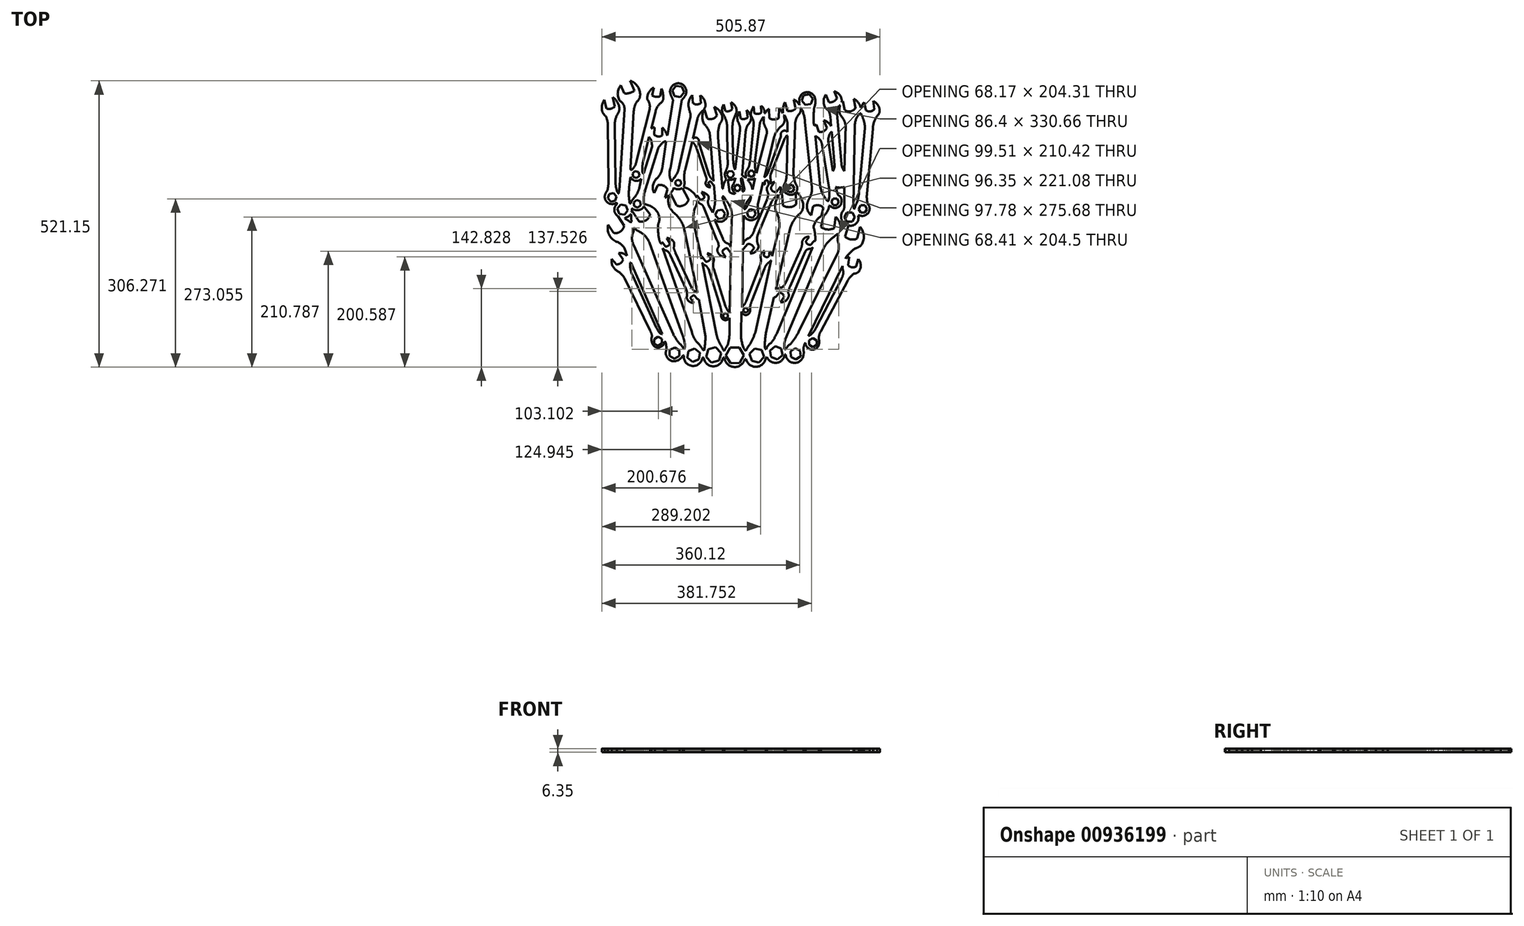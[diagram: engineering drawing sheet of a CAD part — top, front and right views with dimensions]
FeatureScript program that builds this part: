
annotation { "Feature Type Name" : "Feature", "Feature Type Description" : "" }
export const myFeature = defineFeature(function(context is Context, id is Id, definition is map)
    precondition{}
    {
        {
            var Q0;
            Q0=qCreatedBy(makeId("Top.planeOp"),FACE);
            var sketch = newSketch(context, id + "F0", { "sketchPlane" : qUnion([Q0])});
            skArc(sketch, "E0", {"start": v(348.41, 319.52) * mm, "mid": v(345.14, 328.83) * mm, "end": v(339.54, 336.96) * mm});
            skArc(sketch, "E1", {"start": v(301.1, 338.35) * mm, "mid": v(296.53, 329.72) * mm, "end": v(294.36, 320.2) * mm});
            skArc(sketch, "E2", {"start": v(337.47, 296.03) * mm, "mid": v(341.94, 301.33) * mm, "end": v(345.43, 307.32) * mm});
            skArc(sketch, "E3", {"start": v(337.47, 296.03) * mm, "mid": v(335.23, 290) * mm, "end": v(333.28, 283.88) * mm});
            skArc(sketch, "E4", {"start": v(334.87, 283.44) * mm, "mid": v(339.87, 290.96) * mm, "end": v(344.13, 298.93) * mm});
            skArc(sketch, "E5", {"start": v(296.24, 306.6) * mm, "mid": v(300.74, 298.9) * mm, "end": v(305.79, 291.55) * mm});
            skArc(sketch, "E6", {"start": v(310.85, 274.47) * mm, "mid": v(309.33, 283.31) * mm, "end": v(305.79, 291.55) * mm});
            skArc(sketch, "E7", {"start": v(306.8, 314.26) * mm, "mid": v(311.46, 312) * mm, "end": v(316.64, 311.85) * mm});
            skArc(sketch, "E8", {"start": v(330.67, 315.56) * mm, "mid": v(332.7, 316.57) * mm, "end": v(333.7, 318.6) * mm});
            skArc(sketch, "E9", {"start": v(344.13, 298.93) * mm, "mid": v(345.23, 303.05) * mm, "end": v(345.43, 307.32) * mm});
            skArc(sketch, "E10", {"start": v(293.49, 306.6) * mm, "mid": v(296.8, 294.77) * mm, "end": v(301.16, 283.3) * mm});
            skArc(sketch, "E11", {"start": v(294.65, 261.6) * mm, "mid": v(302.74, 271) * mm, "end": v(301.16, 283.3) * mm});
            skArc(sketch, "E12", {"start": v(279.6, 264.35) * mm, "mid": v(286.74, 260.86) * mm, "end": v(294.65, 261.6) * mm});
            skArc(sketch, "E13", {"start": v(276.27, 277.08) * mm, "mid": v(278.22, 284.26) * mm, "end": v(279.74, 291.55) * mm});
            skArc(sketch, "E14", {"start": v(279.74, 291.55) * mm, "mid": v(280.35, 299.07) * mm, "end": v(279.74, 306.6) * mm});
            skArc(sketch, "E15", {"start": v(268.46, 307.32) * mm, "mid": v(262.9, 312.12) * mm, "end": v(256.01, 314.7) * mm});
            skArc(sketch, "E16", {"start": v(267.59, 298.93) * mm, "mid": v(268.55, 303.07) * mm, "end": v(268.46, 307.32) * mm});
            skArc(sketch, "E17", {"start": v(267.59, 298.93) * mm, "mid": v(267.5, 294.82) * mm, "end": v(268.46, 290.82) * mm});
            skArc(sketch, "E18", {"start": v(253.56, 300.73) * mm, "mid": v(258.48, 302.2) * mm, "end": v(261.15, 306.6) * mm});
            skArc(sketch, "E19", {"start": v(247.62, 308.48) * mm, "mid": v(246.88, 306.78) * mm, "end": v(246.75, 304.93) * mm});
            skArc(sketch, "E20", {"start": v(247.98, 298.93) * mm, "mid": v(251.3, 294.76) * mm, "end": v(255.94, 292.13) * mm});
            skArc(sketch, "E21", {"start": v(259.34, 286.92) * mm, "mid": v(258, 289.76) * mm, "end": v(255.94, 292.13) * mm});
            skArc(sketch, "E22", {"start": v(313.82, 329.47) * mm, "mid": v(311.43, 321.31) * mm, "end": v(315.73, 313.98) * mm});
            skArc(sketch, "E23", {"start": v(313.82, 329.47) * mm, "mid": v(315.96, 334.73) * mm, "end": v(317.73, 340.13) * mm});
            skArc(sketch, "E24", {"start": v(327.58, 340.13) * mm, "mid": v(327.99, 333.31) * mm, "end": v(329.86, 326.74) * mm});
            skArc(sketch, "E25", {"start": v(330.22, 319.05) * mm, "mid": v(330.85, 322.93) * mm, "end": v(329.86, 326.74) * mm});
            skArc(sketch, "E26", {"start": v(303.54, 337.46) * mm, "mid": v(310.95, 337.13) * mm, "end": v(317.73, 340.13) * mm});
            skArc(sketch, "E27", {"start": v(298.87, 350.8) * mm, "mid": v(298.22, 344.26) * mm, "end": v(301.1, 338.35) * mm});
            skArc(sketch, "E28", {"start": v(298.87, 350.8) * mm, "mid": v(301.1, 356.06) * mm, "end": v(302.9, 361.48) * mm});
            skArc(sketch, "E29", {"start": v(313.82, 366.87) * mm, "mid": v(314.7, 360.94) * mm, "end": v(316.67, 355.27) * mm});
            skArc(sketch, "E30", {"start": v(339.35, 355.66) * mm, "mid": v(335.97, 349.35) * mm, "end": v(337.47, 342.35) * mm});
            skArc(sketch, "E31", {"start": v(340.94, 338.35) * mm, "mid": v(347.28, 337.45) * mm, "end": v(353.1, 340.13) * mm});
            skArc(sketch, "E32", {"start": v(353.24, 372.16) * mm, "mid": v(353.14, 360.37) * mm, "end": v(355.7, 348.86) * mm});
            skArc(sketch, "E33", {"start": v(339.35, 355.66) * mm, "mid": v(342.59, 363.96) * mm, "end": v(344.13, 372.73) * mm});
            skArc(sketch, "E34", {"start": v(302.9, 361.48) * mm, "mid": v(303.47, 368.7) * mm, "end": v(302.9, 375.92) * mm});
            skArc(sketch, "E35", {"start": v(312.8, 384.02) * mm, "mid": v(313, 375.43) * mm, "end": v(313.82, 366.87) * mm});
            skLineSegment(sketch, "E36", {"start": v(293.12, 324.7) * mm, "end": v(285.89, 414.11) * mm});
            skArc(sketch, "E37", {"start": v(289.21, 439.87) * mm, "mid": v(286.2, 427.16) * mm, "end": v(285.89, 414.11) * mm});
            skArc(sketch, "E38", {"start": v(289.21, 439.87) * mm, "mid": v(293.4, 447.66) * mm, "end": v(291.82, 456.36) * mm});
            skArc(sketch, "E39", {"start": v(291.82, 456.36) * mm, "mid": v(286.63, 464.31) * mm, "end": v(278.8, 469.67) * mm});
            skArc(sketch, "E40", {"start": v(266.06, 448.7) * mm, "mid": v(275.84, 447.87) * mm, "end": v(283.57, 453.9) * mm});
            skArc(sketch, "E41", {"start": v(260.71, 464.46) * mm, "mid": v(257.05, 451.39) * mm, "end": v(260.57, 438.28) * mm});
            skArc(sketch, "E42", {"start": v(270.55, 421.5) * mm, "mid": v(266.58, 430.5) * mm, "end": v(260.57, 438.28) * mm});
            skArc(sketch, "E43", {"start": v(271.56, 410.5) * mm, "mid": v(271.08, 416) * mm, "end": v(270.55, 421.5) * mm});
            skArc(sketch, "E44", {"start": v(296.16, 474.16) * mm, "mid": v(292.96, 464.62) * mm, "end": v(295.58, 454.91) * mm});
            skArc(sketch, "E45", {"start": v(302.1, 435.96) * mm, "mid": v(300.08, 445.87) * mm, "end": v(295.58, 454.91) * mm});
            skArc(sketch, "E46", {"start": v(319.6, 461.28) * mm, "mid": v(316.84, 471.13) * mm, "end": v(309.18, 477.92) * mm});
            skArc(sketch, "E47", {"start": v(319.6, 461.28) * mm, "mid": v(316.27, 452.84) * mm, "end": v(313.09, 444.35) * mm});
            skArc(sketch, "E48", {"start": v(313.09, 444.35) * mm, "mid": v(312.15, 437.27) * mm, "end": v(311.93, 430.13) * mm});
            skArc(sketch, "E49", {"start": v(324.69, 461.28) * mm, "mid": v(320.94, 451.94) * mm, "end": v(322.32, 441.98) * mm});
            skArc(sketch, "E50", {"start": v(345.93, 449.45) * mm, "mid": v(343.47, 457.32) * mm, "end": v(338, 463.49) * mm});
            skArc(sketch, "E51", {"start": v(326.79, 448.45) * mm, "mid": v(333.43, 447.49) * mm, "end": v(339.46, 450.46) * mm});
            skArc(sketch, "E52", {"start": v(340.96, 438.28) * mm, "mid": v(344.53, 443.38) * mm, "end": v(345.93, 449.45) * mm});
            skArc(sketch, "E53", {"start": v(340.96, 438.28) * mm, "mid": v(337.48, 431.75) * mm, "end": v(336.08, 424.49) * mm});
            skArc(sketch, "E54", {"start": v(325.79, 426.42) * mm, "mid": v(325.3, 434.48) * mm, "end": v(322.32, 441.98) * mm});
            skArc(sketch, "E55", {"start": v(350.58, 470.44) * mm, "mid": v(346.67, 463.13) * mm, "end": v(345.52, 454.91) * mm});
            skArc(sketch, "E56", {"start": v(370.45, 458.52) * mm, "mid": v(368.89, 465.9) * mm, "end": v(363.98, 471.64) * mm});
            skArc(sketch, "E57", {"start": v(368.54, 451.86) * mm, "mid": v(364.68, 446.11) * mm, "end": v(361.7, 439.87) * mm});
            skArc(sketch, "E58", {"start": v(378.38, 465.9) * mm, "mid": v(374.32, 462.84) * mm, "end": v(371.82, 458.43) * mm});
            skArc(sketch, "E59", {"start": v(402.9, 458.52) * mm, "mid": v(400.52, 463.04) * mm, "end": v(396.8, 466.54) * mm});
            skArc(sketch, "E60", {"start": v(378.84, 449.45) * mm, "mid": v(387.63, 446.57) * mm, "end": v(396.43, 449.45) * mm});
            skArc(sketch, "E61", {"start": v(351.86, 458.06) * mm, "mid": v(358.26, 456.75) * mm, "end": v(364.25, 459.34) * mm});
            skArc(sketch, "E62", {"start": v(350.58, 436.37) * mm, "mid": v(350.13, 443.75) * mm, "end": v(347.3, 450.59) * mm});
            skArc(sketch, "E63", {"start": v(345.52, 454.91) * mm, "mid": v(346.34, 452.72) * mm, "end": v(347.3, 450.59) * mm});
            skArc(sketch, "E64", {"start": v(369.28, 449.45) * mm, "mid": v(368.87, 440.63) * mm, "end": v(372.18, 432.45) * mm});
            skArc(sketch, "E65", {"start": v(374.19, 419.5) * mm, "mid": v(374.4, 426.17) * mm, "end": v(372.18, 432.45) * mm});
            skArc(sketch, "E66", {"start": v(399.98, 434) * mm, "mid": v(392.86, 425.57) * mm, "end": v(387.95, 415.68) * mm});
            skArc(sketch, "E67", {"start": v(399.98, 434) * mm, "mid": v(403.78, 437.5) * mm, "end": v(406.36, 441.98) * mm});
            skArc(sketch, "E68", {"start": v(406.36, 441.98) * mm, "mid": v(406.7, 447.8) * mm, "end": v(405.18, 453.41) * mm});
            skArc(sketch, "E69", {"start": v(412.29, 438.28) * mm, "mid": v(410.3, 446.94) * mm, "end": v(406.36, 454.91) * mm});
            skArc(sketch, "E70", {"start": v(431.7, 454.91) * mm, "mid": v(427.44, 446.06) * mm, "end": v(425.78, 436.37) * mm});
            skArc(sketch, "E71", {"start": v(431.7, 454.91) * mm, "mid": v(435.63, 460.62) * mm, "end": v(436.08, 467.54) * mm});
            skArc(sketch, "E72", {"start": v(407.37, 478.2) * mm, "mid": v(404.3, 469.07) * mm, "end": v(404.08, 459.43) * mm});
            skArc(sketch, "E73", {"start": v(412.29, 462.34) * mm, "mid": v(420.27, 462.54) * mm, "end": v(426.96, 466.9) * mm});
            skArc(sketch, "E74", {"start": v(433.78, 473.03) * mm, "mid": v(429.5, 479.16) * mm, "end": v(423.3, 483.37) * mm});
            skArc(sketch, "E75", {"start": v(433.66, 482.22) * mm, "mid": v(433.42, 478.39) * mm, "end": v(434.24, 474.64) * mm});
            skArc(sketch, "E76", {"start": v(462.49, 484.05) * mm, "mid": v(447.22, 496.46) * mm, "end": v(433.66, 482.22) * mm});
            skArc(sketch, "E77", {"start": v(460.53, 467.06) * mm, "mid": v(462.58, 475.43) * mm, "end": v(462.49, 484.05) * mm});
            skArc(sketch, "E78", {"start": v(460.53, 467.06) * mm, "mid": v(459.75, 453.95) * mm, "end": v(459.76, 440.82) * mm});
            skArc(sketch, "E79", {"start": v(444.03, 441.57) * mm, "mid": v(441.93, 455.04) * mm, "end": v(436.85, 467.7) * mm});
            skLineSegment(sketch, "E80", {"start": v(487.6, 478.07) * mm, "end": v(482.07, 492.23) * mm});
            skLineSegment(sketch, "E81", {"start": v(502, 485.54) * mm, "end": v(497.12, 498.05) * mm});
            skArc(sketch, "E82", {"start": v(482.07, 492.23) * mm, "mid": v(477.94, 481.37) * mm, "end": v(480.01, 469.94) * mm});
            skArc(sketch, "E83", {"start": v(510.73, 483.24) * mm, "mid": v(506.12, 492.67) * mm, "end": v(497.12, 498.05) * mm});
            skArc(sketch, "E84", {"start": v(487.6, 478.07) * mm, "mid": v(495.95, 479.6) * mm, "end": v(502, 485.54) * mm});
            skArc(sketch, "E85", {"start": v(480.01, 469.94) * mm, "mid": v(482.45, 466.43) * mm, "end": v(486.03, 464.1) * mm});
            skArc(sketch, "E86", {"start": v(510.73, 478.87) * mm, "mid": v(510.92, 481.06) * mm, "end": v(510.73, 483.24) * mm});
            skArc(sketch, "E87", {"start": v(506.35, 472.22) * mm, "mid": v(503.02, 464.98) * mm, "end": v(502, 457.09) * mm});
            skArc(sketch, "E88", {"start": v(490.04, 452.53) * mm, "mid": v(488.6, 458.51) * mm, "end": v(486.03, 464.1) * mm});
            skArc(sketch, "E89", {"start": v(508.08, 472.13) * mm, "mid": v(506.38, 462.88) * mm, "end": v(509.18, 453.9) * mm});
            skArc(sketch, "E90", {"start": v(516.2, 464.1) * mm, "mid": v(526.97, 461.6) * mm, "end": v(535.98, 468.02) * mm});
            skArc(sketch, "E91", {"start": v(545.36, 468.48) * mm, "mid": v(540.69, 477.86) * mm, "end": v(532.6, 484.52) * mm});
            skArc(sketch, "E92", {"start": v(551.56, 478.07) * mm, "mid": v(548.48, 473.5) * mm, "end": v(546.64, 468.3) * mm});
            skArc(sketch, "E93", {"start": v(517.84, 436.03) * mm, "mid": v(514.76, 445.57) * mm, "end": v(509.18, 453.9) * mm});
            skArc(sketch, "E94", {"start": v(543.81, 457.75) * mm, "mid": v(537.4, 448.01) * mm, "end": v(534.7, 436.67) * mm});
            skArc(sketch, "E95", {"start": v(546.1, 457.75) * mm, "mid": v(547.28, 454.14) * mm, "end": v(549.1, 450.8) * mm});
            skArc(sketch, "E96", {"start": v(553.2, 431.02) * mm, "mid": v(552, 441.08) * mm, "end": v(549.1, 450.8) * mm});
            skArc(sketch, "E97", {"start": v(575.44, 452.98) * mm, "mid": v(569.66, 442.09) * mm, "end": v(567.6, 429.92) * mm});
            skArc(sketch, "E98", {"start": v(575.44, 452.98) * mm, "mid": v(579.58, 459.64) * mm, "end": v(579.27, 467.48) * mm});
            skArc(sketch, "E99", {"start": v(579.27, 467.48) * mm, "mid": v(575.1, 475.08) * mm, "end": v(568.21, 480.33) * mm});
            skArc(sketch, "E100", {"start": v(555.02, 463.28) * mm, "mid": v(563, 461.47) * mm, "end": v(570.06, 465.56) * mm});
            skArc(sketch, "E101", {"start": v(491.17, 434.69) * mm, "mid": v(485.9, 441.28) * mm, "end": v(478.32, 445) * mm});
            skArc(sketch, "E102", {"start": v(469.3, 424.22) * mm, "mid": v(477.82, 425.25) * mm, "end": v(483.88, 431.33) * mm});
            skLineSegment(sketch, "E103", {"start": v(469.3, 424.22) * mm, "end": v(464.75, 437.26) * mm});
            skLineSegment(sketch, "E104", {"start": v(483.88, 431.33) * mm, "end": v(478.32, 445) * mm});
            skLineSegment(sketch, "E105", {"start": v(491.17, 434.69) * mm, "end": v(490.04, 452.53) * mm});
            skLineSegment(sketch, "E106", {"start": v(459.76, 440.82) * mm, "end": v(461.2, 435.27) * mm});
            skLineSegment(sketch, "E107", {"start": v(464.75, 437.26) * mm, "end": v(461.2, 435.27) * mm});
            skLineSegment(sketch, "E108", {"start": v(502, 457.09) * mm, "end": v(510.43, 365.53) * mm});
            skLineSegment(sketch, "E109", {"start": v(497.77, 363.22) * mm, "end": v(492.47, 424.42) * mm});
            skLineSegment(sketch, "E110", {"start": v(517.84, 436.03) * mm, "end": v(515.43, 353.09) * mm});
            skLineSegment(sketch, "E111", {"start": v(534.7, 436.67) * mm, "end": v(532.32, 291.07) * mm});
            skLineSegment(sketch, "E112", {"start": v(542.45, 314.37) * mm, "end": v(553.2, 431.02) * mm});
            skLineSegment(sketch, "E113", {"start": v(567.6, 429.92) * mm, "end": v(556.7, 311.62) * mm});
            skLineSegment(sketch, "E114", {"start": v(494.85, 353.19) * mm, "end": v(486.7, 404.52) * mm});
            skLineSegment(sketch, "E115", {"start": v(474.87, 401.42) * mm, "end": v(487.96, 319.3) * mm});
            skLineSegment(sketch, "E116", {"start": v(471.93, 323.62) * mm, "end": v(462.81, 417.09) * mm});
            skLineSegment(sketch, "E117", {"start": v(444.03, 441.57) * mm, "end": v(456.39, 323.43) * mm});
            skArc(sketch, "E118", {"start": v(474.87, 401.42) * mm, "mid": v(472.33, 408.49) * mm, "end": v(467.39, 414.15) * mm});
            skArc(sketch, "E119", {"start": v(462.81, 417.09) * mm, "mid": v(465, 415.47) * mm, "end": v(467.39, 414.15) * mm});
            skArc(sketch, "E120", {"start": v(490.01, 422.07) * mm, "mid": v(486.83, 413.58) * mm, "end": v(486.7, 404.52) * mm});
            skArc(sketch, "E121", {"start": v(492.47, 424.42) * mm, "mid": v(491.1, 423.39) * mm, "end": v(490.01, 422.07) * mm});
            skArc(sketch, "E122", {"start": v(508.08, 472.13) * mm, "mid": v(507.23, 472.4) * mm, "end": v(506.35, 472.22) * mm});
            skArc(sketch, "E123", {"start": v(513.27, 479.88) * mm, "mid": v(511.9, 479.64) * mm, "end": v(510.73, 478.87) * mm});
            skLineSegment(sketch, "E124", {"start": v(513.27, 479.88) * mm, "end": v(516.2, 464.1) * mm});
            skLineSegment(sketch, "E125", {"start": v(535.98, 468.02) * mm, "end": v(532.6, 484.52) * mm});
            skLineSegment(sketch, "E126", {"start": v(545.36, 468.48) * mm, "end": v(546.64, 468.3) * mm});
            skLineSegment(sketch, "E127", {"start": v(543.81, 457.75) * mm, "end": v(546.1, 457.75) * mm});
            skLineSegment(sketch, "E128", {"start": v(555.02, 463.28) * mm, "end": v(551.56, 478.07) * mm});
            skLineSegment(sketch, "E129", {"start": v(570.06, 465.56) * mm, "end": v(568.21, 480.33) * mm});
            skLineSegment(sketch, "E130", {"start": v(436.85, 467.7) * mm, "end": v(436.08, 467.54) * mm});
            skLineSegment(sketch, "E131", {"start": v(434.24, 474.64) * mm, "end": v(433.78, 473.03) * mm});
            skLineSegment(sketch, "E132", {"start": v(426.96, 466.9) * mm, "end": v(423.3, 483.37) * mm});
            skLineSegment(sketch, "E133", {"start": v(412.29, 462.34) * mm, "end": v(407.37, 478.2) * mm});
            skLineSegment(sketch, "E134", {"start": v(404.08, 459.43) * mm, "end": v(402.9, 458.52) * mm});
            skLineSegment(sketch, "E135", {"start": v(406.36, 454.91) * mm, "end": v(405.18, 453.41) * mm});
            skLineSegment(sketch, "E136", {"start": v(396.43, 449.45) * mm, "end": v(396.8, 466.54) * mm});
            skLineSegment(sketch, "E137", {"start": v(378.84, 449.45) * mm, "end": v(378.38, 465.9) * mm});
            skLineSegment(sketch, "E138", {"start": v(425.78, 436.37) * mm, "end": v(423.1, 350.19) * mm});
            skLineSegment(sketch, "E139", {"start": v(410.85, 350.19) * mm, "end": v(411.98, 416.8) * mm});
            skLineSegment(sketch, "E140", {"start": v(412.29, 438.28) * mm, "end": v(412.29, 424.61) * mm});
            skArc(sketch, "E141", {"start": v(423.1, 350.19) * mm, "mid": v(423.95, 339.63) * mm, "end": v(427.1, 329.52) * mm});
            skArc(sketch, "E142", {"start": v(428.13, 315.16) * mm, "mid": v(429.89, 322.5) * mm, "end": v(427.1, 329.52) * mm});
            skArc(sketch, "E143", {"start": v(440.77, 287.6) * mm, "mid": v(437.57, 302.81) * mm, "end": v(428.13, 315.16) * mm});
            skArc(sketch, "E144", {"start": v(430.66, 272.1) * mm, "mid": v(437.52, 278.68) * mm, "end": v(440.77, 287.6) * mm});
            skArc(sketch, "E145", {"start": v(430.66, 272.1) * mm, "mid": v(422.74, 261.56) * mm, "end": v(417.23, 249.6) * mm});
            skArc(sketch, "E146", {"start": v(448.22, 293.75) * mm, "mid": v(448.68, 281.86) * mm, "end": v(455.51, 272.1) * mm});
            skArc(sketch, "E147", {"start": v(452.23, 303.5) * mm, "mid": v(449.82, 298.8) * mm, "end": v(448.22, 293.75) * mm});
            skArc(sketch, "E148", {"start": v(452.23, 303.5) * mm, "mid": v(455.86, 313.14) * mm, "end": v(456.39, 323.43) * mm});
            skArc(sketch, "E149", {"start": v(471.93, 323.62) * mm, "mid": v(476.88, 310) * mm, "end": v(485.22, 298.13) * mm});
            skArc(sketch, "E150", {"start": v(486.77, 299.31) * mm, "mid": v(488.46, 309.25) * mm, "end": v(487.96, 319.3) * mm});
            skArc(sketch, "E151", {"start": v(485.22, 298.13) * mm, "mid": v(486.23, 298.42) * mm, "end": v(486.77, 299.31) * mm});
            skArc(sketch, "E152", {"start": v(477.47, 285.72) * mm, "mid": v(468.21, 290.63) * mm, "end": v(458.18, 287.6) * mm});
            skArc(sketch, "E153", {"start": v(403.84, 290.12) * mm, "mid": v(416.36, 287.2) * mm, "end": v(428.13, 292.37) * mm});
            skArc(sketch, "E154", {"start": v(404.86, 323.43) * mm, "mid": v(412.52, 310.76) * mm, "end": v(427.1, 313.35) * mm});
            skArc(sketch, "E155", {"start": v(408.47, 333.02) * mm, "mid": v(406.08, 328.45) * mm, "end": v(404.86, 323.43) * mm});
            skArc(sketch, "E156", {"start": v(408.47, 333.02) * mm, "mid": v(410.18, 341.53) * mm, "end": v(410.85, 350.19) * mm});
            skArc(sketch, "E157", {"start": v(401.75, 313.43) * mm, "mid": v(400.29, 312.91) * mm, "end": v(398.85, 312.35) * mm});
            skArc(sketch, "E158", {"start": v(398.85, 312.35) * mm, "mid": v(400.24, 318.27) * mm, "end": v(399.36, 324.28) * mm});
            skArc(sketch, "E159", {"start": v(382.11, 323.43) * mm, "mid": v(385.04, 316.56) * mm, "end": v(392.38, 315.16) * mm});
            skArc(sketch, "E160", {"start": v(388.62, 333.02) * mm, "mid": v(384.26, 331.75) * mm, "end": v(380.3, 329.52) * mm});
            skArc(sketch, "E161", {"start": v(379.5, 330.14) * mm, "mid": v(381.54, 334.6) * mm, "end": v(380.88, 339.47) * mm});
            skArc(sketch, "E162", {"start": v(381.82, 347.21) * mm, "mid": v(380.86, 343.4) * mm, "end": v(380.88, 339.47) * mm});
            skArc(sketch, "E163", {"start": v(410.85, 417.67) * mm, "mid": v(408.91, 414.85) * mm, "end": v(407.21, 411.88) * mm});
            skArc(sketch, "E164", {"start": v(411.98, 424.25) * mm, "mid": v(405.3, 426.26) * mm, "end": v(400.27, 421.43) * mm});
            skArc(sketch, "E165", {"start": v(400.27, 421.43) * mm, "mid": v(399.81, 418.46) * mm, "end": v(400.27, 415.5) * mm});
            skArc(sketch, "E166", {"start": v(372.42, 343.47) * mm, "mid": v(371.17, 342.67) * mm, "end": v(370.03, 341.73) * mm});
            skArc(sketch, "E167", {"start": v(372.42, 343.47) * mm, "mid": v(374.38, 345.86) * mm, "end": v(375.67, 348.68) * mm});
            skArc(sketch, "E168", {"start": v(377.2, 334.79) * mm, "mid": v(374.06, 335.66) * mm, "end": v(370.97, 334.64) * mm});
            skArc(sketch, "E169", {"start": v(367.42, 332.25) * mm, "mid": v(368.62, 329.82) * mm, "end": v(370.68, 328.06) * mm});
            skArc(sketch, "E170", {"start": v(377.77, 327.48) * mm, "mid": v(374.55, 320.7) * mm, "end": v(376.76, 313.52) * mm});
            skArc(sketch, "E171", {"start": v(374.59, 300.2) * mm, "mid": v(376.5, 306.73) * mm, "end": v(376.76, 313.52) * mm});
            skArc(sketch, "E172", {"start": v(395.5, 309.03) * mm, "mid": v(388.15, 303.82) * mm, "end": v(382.98, 296.44) * mm});
            skArc(sketch, "E173", {"start": v(396.5, 307.87) * mm, "mid": v(390.36, 294.35) * mm, "end": v(391.3, 279.52) * mm});
            skArc(sketch, "E174", {"start": v(397.3, 251.01) * mm, "mid": v(396.3, 265.69) * mm, "end": v(391.3, 279.52) * mm});
            skArc(sketch, "E175", {"start": v(384.18, 198.36) * mm, "mid": v(382.62, 203.05) * mm, "end": v(379.54, 206.93) * mm});
            skArc(sketch, "E176", {"start": v(369.15, 198.9) * mm, "mid": v(373.53, 196.23) * mm, "end": v(378.53, 197.36) * mm});
            skArc(sketch, "E177", {"start": v(370.15, 207.75) * mm, "mid": v(363.78, 201.36) * mm, "end": v(363.95, 192.34) * mm});
            skArc(sketch, "E178", {"start": v(375.34, 184.41) * mm, "mid": v(379.03, 187.17) * mm, "end": v(382.09, 190.61) * mm});
            skArc(sketch, "E179", {"start": v(375.34, 184.41) * mm, "mid": v(372.38, 180.05) * mm, "end": v(370.06, 175.3) * mm});
            skArc(sketch, "E180", {"start": v(361.76, 180.5) * mm, "mid": v(363.42, 186.32) * mm, "end": v(363.95, 192.34) * mm});
            skArc(sketch, "E181", {"start": v(344.06, 202.97) * mm, "mid": v(354.7, 206.9) * mm, "end": v(359.54, 217.15) * mm});
            skArc(sketch, "E182", {"start": v(359.54, 239.58) * mm, "mid": v(356.64, 228.36) * mm, "end": v(359.54, 217.15) * mm});
            skArc(sketch, "E183", {"start": v(342.18, 230.6) * mm, "mid": v(334.85, 226.6) * mm, "end": v(331.04, 219.18) * mm});
            skArc(sketch, "E184", {"start": v(342.18, 230.6) * mm, "mid": v(348.26, 237.5) * mm, "end": v(351.88, 245.94) * mm});
            skArc(sketch, "E185", {"start": v(351.15, 212.66) * mm, "mid": v(346.78, 218.47) * mm, "end": v(339.72, 220.19) * mm});
            skArc(sketch, "E186", {"start": v(332.75, 272.1) * mm, "mid": v(346.84, 263.34) * mm, "end": v(359.54, 274.01) * mm});
            skArc(sketch, "E187", {"start": v(357.92, 291.95) * mm, "mid": v(358.2, 282.94) * mm, "end": v(359.54, 274.01) * mm});
            skArc(sketch, "E188", {"start": v(333.28, 283.88) * mm, "mid": v(334, 283.41) * mm, "end": v(334.87, 283.44) * mm});
            skArc(sketch, "E189", {"start": v(330.22, 319.05) * mm, "mid": v(330.21, 317.28) * mm, "end": v(330.67, 315.56) * mm});
            skArc(sketch, "E190", {"start": v(316.64, 311.85) * mm, "mid": v(316.48, 313.04) * mm, "end": v(315.73, 313.98) * mm});
            skLineSegment(sketch, "E191", {"start": v(455.51, 272.1) * mm, "end": v(458.18, 287.6) * mm});
            skLineSegment(sketch, "E192", {"start": v(403.84, 290.12) * mm, "end": v(401.75, 313.43) * mm});
            skLineSegment(sketch, "E193", {"start": v(428.13, 292.37) * mm, "end": v(427.1, 313.35) * mm});
            skLineSegment(sketch, "E194", {"start": v(392.38, 315.16) * mm, "end": v(399.36, 324.28) * mm});
            skLineSegment(sketch, "E195", {"start": v(382.11, 323.43) * mm, "end": v(388.62, 333.02) * mm});
            skLineSegment(sketch, "E196", {"start": v(370.68, 328.06) * mm, "end": v(370.97, 334.64) * mm});
            skLineSegment(sketch, "E197", {"start": v(377.2, 334.79) * mm, "end": v(377.77, 327.48) * mm});
            skLineSegment(sketch, "E198", {"start": v(380.3, 329.52) * mm, "end": v(379.5, 330.14) * mm});
            skLineSegment(sketch, "E199", {"start": v(381.82, 347.21) * mm, "end": v(407.21, 411.88) * mm});
            skLineSegment(sketch, "E200", {"start": v(375.67, 348.68) * mm, "end": v(400.27, 415.5) * mm});
            skLineSegment(sketch, "E201", {"start": v(387.95, 415.68) * mm, "end": v(370.03, 341.73) * mm});
            skLineSegment(sketch, "E202", {"start": v(357.92, 291.95) * mm, "end": v(367.42, 332.25) * mm});
            skLineSegment(sketch, "E203", {"start": v(374.59, 300.2) * mm, "end": v(351.88, 245.94) * mm});
            skLineSegment(sketch, "E204", {"start": v(359.54, 239.58) * mm, "end": v(382.98, 296.44) * mm});
            skLineSegment(sketch, "E205", {"start": v(397.3, 251.01) * mm, "end": v(384.18, 197.84) * mm});
            skLineSegment(sketch, "E206", {"start": v(384.18, 197.84) * mm, "end": v(384.18, 198.36) * mm});
            skLineSegment(sketch, "E207", {"start": v(417.23, 249.6) * mm, "end": v(391.07, 138.2) * mm});
            skLineSegment(sketch, "E208", {"start": v(396.5, 307.87) * mm, "end": v(395.5, 309.03) * mm});
            skLineSegment(sketch, "E209", {"start": v(374.19, 419.5) * mm, "end": v(355.7, 348.86) * mm});
            skLineSegment(sketch, "E210", {"start": v(353.24, 372.16) * mm, "end": v(361.7, 439.87) * mm});
            skLineSegment(sketch, "E211", {"start": v(350.58, 436.37) * mm, "end": v(344.13, 372.73) * mm});
            skLineSegment(sketch, "E212", {"start": v(329.58, 344.79) * mm, "end": v(336.08, 424.49) * mm});
            skLineSegment(sketch, "E213", {"start": v(325.79, 426.42) * mm, "end": v(316.67, 355.27) * mm});
            skLineSegment(sketch, "E214", {"start": v(312.8, 384.02) * mm, "end": v(311.93, 430.13) * mm});
            skLineSegment(sketch, "E215", {"start": v(302.1, 435.96) * mm, "end": v(302.9, 375.92) * mm});
            skLineSegment(sketch, "E216", {"start": v(369.28, 449.45) * mm, "end": v(368.54, 451.86) * mm});
            skLineSegment(sketch, "E217", {"start": v(371.82, 458.43) * mm, "end": v(370.45, 458.52) * mm});
            skLineSegment(sketch, "E218", {"start": v(364.25, 459.34) * mm, "end": v(363.98, 471.64) * mm});
            skLineSegment(sketch, "E219", {"start": v(351.86, 458.06) * mm, "end": v(350.58, 470.44) * mm});
            skLineSegment(sketch, "E220", {"start": v(339.46, 450.46) * mm, "end": v(338, 463.49) * mm});
            skLineSegment(sketch, "E221", {"start": v(326.79, 448.45) * mm, "end": v(324.69, 461.28) * mm});
            skLineSegment(sketch, "E222", {"start": v(311.93, 466) * mm, "end": v(309.18, 477.92) * mm});
            skLineSegment(sketch, "E223", {"start": v(299.31, 462.09) * mm, "end": v(296.16, 474.16) * mm});
            skArc(sketch, "E224", {"start": v(299.31, 462.09) * mm, "mid": v(306.22, 462.09) * mm, "end": v(311.93, 466) * mm});
            skLineSegment(sketch, "E225", {"start": v(283.57, 453.9) * mm, "end": v(278.8, 469.67) * mm});
            skLineSegment(sketch, "E226", {"start": v(266.06, 448.7) * mm, "end": v(260.71, 464.46) * mm});
            skLineSegment(sketch, "E227", {"start": v(254.3, 476.39) * mm, "end": v(253.5, 490.42) * mm});
            skArc(sketch, "E228", {"start": v(262.73, 473.1) * mm, "mid": v(260.38, 482.97) * mm, "end": v(253.5, 490.42) * mm});
            skArc(sketch, "E229", {"start": v(238.73, 491.18) * mm, "mid": v(233.1, 481.8) * mm, "end": v(232.01, 470.92) * mm});
            skArc(sketch, "E230", {"start": v(239.94, 476.26) * mm, "mid": v(247.14, 474.18) * mm, "end": v(254.3, 476.39) * mm});
            skLineSegment(sketch, "E231", {"start": v(238.73, 491.18) * mm, "end": v(239.94, 476.26) * mm});
            skArc(sketch, "E232", {"start": v(256.93, 461.91) * mm, "mid": v(261.24, 466.77) * mm, "end": v(262.73, 473.1) * mm});
            skArc(sketch, "E233", {"start": v(256.93, 461.91) * mm, "mid": v(251.62, 455.62) * mm, "end": v(247.96, 448.24) * mm});
            skArc(sketch, "E234", {"start": v(232.01, 470.92) * mm, "mid": v(233.54, 463.65) * mm, "end": v(235.73, 456.56) * mm});
            skArc(sketch, "E235", {"start": v(234.57, 446.65) * mm, "mid": v(235.4, 451.58) * mm, "end": v(235.73, 456.56) * mm});
            skArc(sketch, "E236", {"start": v(250.41, 405.56) * mm, "mid": v(247.93, 412.95) * mm, "end": v(240.21, 411.78) * mm});
            skArc(sketch, "E237", {"start": v(238.48, 406.93) * mm, "mid": v(239.73, 404.62) * mm, "end": v(241.88, 403.1) * mm});
            skArc(sketch, "E238", {"start": v(277.52, 334.72) * mm, "mid": v(276.16, 337.16) * mm, "end": v(273.83, 338.7) * mm});
            skArc(sketch, "E239", {"start": v(269.49, 345.79) * mm, "mid": v(271.34, 342.05) * mm, "end": v(273.83, 338.7) * mm});
            skArc(sketch, "E240", {"start": v(272.6, 333.78) * mm, "mid": v(269.55, 333.07) * mm, "end": v(267.53, 330.67) * mm});
            skArc(sketch, "E241", {"start": v(263.21, 328.96) * mm, "mid": v(266.5, 324.6) * mm, "end": v(271.83, 323.36) * mm});
            skArc(sketch, "E242", {"start": v(264.8, 336.12) * mm, "mid": v(263.28, 332.7) * mm, "end": v(263.21, 328.96) * mm});
            skArc(sketch, "E243", {"start": v(264.8, 336.12) * mm, "mid": v(264.53, 339.75) * mm, "end": v(263.58, 343.27) * mm});
            skArc(sketch, "E244", {"start": v(245.43, 397.1) * mm, "mid": v(243.84, 400.2) * mm, "end": v(241.88, 403.1) * mm});
            skArc(sketch, "E245", {"start": v(250.41, 405.56) * mm, "mid": v(251.03, 402.87) * mm, "end": v(251.74, 400.2) * mm});
            skArc(sketch, "E246", {"start": v(276.81, 328) * mm, "mid": v(277.62, 327.72) * mm, "end": v(278.3, 328.22) * mm});
            skArc(sketch, "E247", {"start": v(246.75, 304.93) * mm, "mid": v(236.84, 316.68) * mm, "end": v(223.1, 323.56) * mm});
            skArc(sketch, "E248", {"start": v(223.1, 323.56) * mm, "mid": v(224.6, 329.75) * mm, "end": v(224.26, 336.12) * mm});
            skArc(sketch, "E249", {"start": v(225.78, 355.68) * mm, "mid": v(224.28, 345.96) * mm, "end": v(224.26, 336.12) * mm});
            skArc(sketch, "E250", {"start": v(207.17, 342.02) * mm, "mid": v(203.69, 337.89) * mm, "end": v(201.09, 333.15) * mm});
            skArc(sketch, "E251", {"start": v(207.17, 342.02) * mm, "mid": v(211.8, 350.24) * mm, "end": v(214.64, 359.24) * mm});
            skArc(sketch, "E252", {"start": v(205, 322.15) * mm, "mid": v(212.94, 319.79) * mm, "end": v(220.95, 321.92) * mm});
            skArc(sketch, "E253", {"start": v(210.16, 290.11) * mm, "mid": v(223.63, 290.7) * mm, "end": v(232.01, 301.25) * mm});
            skArc(sketch, "E254", {"start": v(196.5, 307.87) * mm, "mid": v(196.25, 290.97) * mm, "end": v(205.45, 276.8) * mm});
            skArc(sketch, "E255", {"start": v(188.9, 304.36) * mm, "mid": v(192.7, 306.15) * mm, "end": v(195.49, 309.28) * mm});
            skArc(sketch, "E256", {"start": v(193.75, 319.33) * mm, "mid": v(186.11, 326.49) * mm, "end": v(175.67, 327.07) * mm});
            skArc(sketch, "E257", {"start": v(173.62, 338.7) * mm, "mid": v(167.15, 326.42) * mm, "end": v(169.52, 312.75) * mm});
            skArc(sketch, "E258", {"start": v(173.62, 338.7) * mm, "mid": v(180.31, 347.27) * mm, "end": v(184, 357.5) * mm});
            skArc(sketch, "E259", {"start": v(199.14, 358.87) * mm, "mid": v(197.47, 345.8) * mm, "end": v(201.09, 333.15) * mm});
            skArc(sketch, "E260", {"start": v(153.84, 319.85) * mm, "mid": v(150.55, 306.38) * mm, "end": v(150.74, 292.52) * mm});
            skArc(sketch, "E261", {"start": v(134.08, 304.93) * mm, "mid": v(129.8, 300.17) * mm, "end": v(126.85, 294.47) * mm});
            skArc(sketch, "E262", {"start": v(134.08, 304.93) * mm, "mid": v(138.8, 312.73) * mm, "end": v(142.35, 321.12) * mm});
            skArc(sketch, "E263", {"start": v(176.92, 275.41) * mm, "mid": v(166, 287.3) * mm, "end": v(150.74, 292.52) * mm});
            skArc(sketch, "E264", {"start": v(176.92, 256.46) * mm, "mid": v(178.95, 265.94) * mm, "end": v(176.92, 275.41) * mm});
            skArc(sketch, "E265", {"start": v(176.92, 256.46) * mm, "mid": v(176.7, 243.22) * mm, "end": v(178.18, 230.05) * mm});
            skArc(sketch, "E266", {"start": v(161.07, 221.55) * mm, "mid": v(153.5, 233.98) * mm, "end": v(142, 242.91) * mm});
            skArc(sketch, "E267", {"start": v(134.08, 249.46) * mm, "mid": v(137.42, 245.43) * mm, "end": v(142, 242.91) * mm});
            skArc(sketch, "E268", {"start": v(142, 261.06) * mm, "mid": v(154.64, 263.31) * mm, "end": v(161.87, 273.92) * mm});
            skArc(sketch, "E269", {"start": v(131.1, 283.68) * mm, "mid": v(141.99, 281.89) * mm, "end": v(150.74, 288.62) * mm});
            skArc(sketch, "E270", {"start": v(128.23, 278.28) * mm, "mid": v(128.78, 280.96) * mm, "end": v(128.46, 283.68) * mm});
            skArc(sketch, "E271", {"start": v(127.65, 273.96) * mm, "mid": v(127.53, 266.89) * mm, "end": v(128.69, 259.9) * mm});
            skArc(sketch, "E272", {"start": v(125.82, 259.9) * mm, "mid": v(121.08, 263.4) * mm, "end": v(115.94, 266.27) * mm});
            skArc(sketch, "E273", {"start": v(116.97, 267.99) * mm, "mid": v(121.9, 270) * mm, "end": v(125.82, 273.62) * mm});
            skArc(sketch, "E274", {"start": v(101.36, 292.52) * mm, "mid": v(96.92, 281.08) * mm, "end": v(103.54, 270.74) * mm});
            skArc(sketch, "E275", {"start": v(79.42, 306.46) * mm, "mid": v(86.8, 294.25) * mm, "end": v(101.01, 295.43) * mm});
            skArc(sketch, "E276", {"start": v(84.25, 317.02) * mm, "mid": v(80.9, 312.16) * mm, "end": v(79.42, 306.46) * mm});
            skArc(sketch, "E277", {"start": v(84.25, 317.02) * mm, "mid": v(85.6, 324.46) * mm, "end": v(86.54, 331.95) * mm});
            skArc(sketch, "E278", {"start": v(99.06, 333.15) * mm, "mid": v(99.96, 323.67) * mm, "end": v(102.73, 314.55) * mm});
            skArc(sketch, "E279", {"start": v(104.57, 311.4) * mm, "mid": v(103.74, 313.02) * mm, "end": v(102.73, 314.55) * mm});
            skArc(sketch, "E280", {"start": v(123.98, 323.56) * mm, "mid": v(123.34, 308.88) * mm, "end": v(125.01, 294.29) * mm});
            skArc(sketch, "E281", {"start": v(104.57, 311.4) * mm, "mid": v(105.88, 319.11) * mm, "end": v(106.64, 326.9) * mm});
            skArc(sketch, "E282", {"start": v(126.4, 342.02) * mm, "mid": v(135.3, 334.96) * mm, "end": v(146.03, 338.7) * mm});
            skArc(sketch, "E283", {"start": v(96.42, 240.08) * mm, "mid": v(108.16, 242.75) * mm, "end": v(114.56, 252.95) * mm});
            skArc(sketch, "E284", {"start": v(129.84, 237.9) * mm, "mid": v(131.95, 242.87) * mm, "end": v(131.44, 248.24) * mm});
            skArc(sketch, "E285", {"start": v(129.84, 237.9) * mm, "mid": v(129.32, 227.18) * mm, "end": v(132.7, 217) * mm});
            skArc(sketch, "E286", {"start": v(116.86, 208.85) * mm, "mid": v(110.07, 218.83) * mm, "end": v(99.52, 224.7) * mm});
            skArc(sketch, "E287", {"start": v(85.62, 254.9) * mm, "mid": v(87.34, 237.39) * mm, "end": v(99.52, 224.7) * mm});
            skArc(sketch, "E288", {"start": v(119.84, 198.51) * mm, "mid": v(112.86, 203) * mm, "end": v(104.57, 203.45) * mm});
            skArc(sketch, "E289", {"start": v(92.05, 193) * mm, "mid": v(93.54, 180.8) * mm, "end": v(101.59, 171.53) * mm});
            skArc(sketch, "E290", {"start": v(101.01, 182.9) * mm, "mid": v(108.45, 185.34) * mm, "end": v(112.95, 191.74) * mm});
            skArc(sketch, "E291", {"start": v(115.37, 157.63) * mm, "mid": v(109.49, 165.58) * mm, "end": v(101.59, 171.53) * mm});
            skArc(sketch, "E292", {"start": v(125.93, 186) * mm, "mid": v(126.37, 174.2) * mm, "end": v(129.84, 162.91) * mm});
            skArc(sketch, "E293", {"start": v(165.54, 52.34) * mm, "mid": v(165.08, 41.96) * mm, "end": v(170.6, 33.16) * mm});
            skArc(sketch, "E294", {"start": v(170.6, 33.16) * mm, "mid": v(181.85, 32.87) * mm, "end": v(187.93, 42.35) * mm});
            skArc(sketch, "E295", {"start": v(173.62, 67.73) * mm, "mid": v(177.4, 61.15) * mm, "end": v(182.65, 55.67) * mm});
            skArc(sketch, "E296", {"start": v(191.76, 27.25) * mm, "mid": v(191.4, 34.54) * mm, "end": v(190.03, 41.71) * mm});
            skArc(sketch, "E297", {"start": v(191.76, 27.25) * mm, "mid": v(197.13, 9.18) * mm, "end": v(215.92, 10.6) * mm});
            skArc(sketch, "E298", {"start": v(215.92, 10.6) * mm, "mid": v(219.38, 13.52) * mm, "end": v(221.42, 17.55) * mm});
            skArc(sketch, "E299", {"start": v(223.3, 16.97) * mm, "mid": v(238.43, -1.86) * mm, "end": v(257.3, 13.21) * mm});
            skArc(sketch, "E300", {"start": v(259.62, 13.21) * mm, "mid": v(277.2, -2.62) * mm, "end": v(294.78, 13.21) * mm});
            skArc(sketch, "E301", {"start": v(297.38, 13.21) * mm, "mid": v(314.71, -3.86) * mm, "end": v(334.28, 10.6) * mm});
            skArc(sketch, "E302", {"start": v(336.6, 10.6) * mm, "mid": v(355.71, -3.47) * mm, "end": v(372.62, 13.21) * mm});
            skArc(sketch, "E303", {"start": v(374.64, 14.51) * mm, "mid": v(392.64, 3.78) * mm, "end": v(407.05, 19) * mm});
            skArc(sketch, "E304", {"start": v(408.79, 18.7) * mm, "mid": v(424.46, 3.6) * mm, "end": v(441.05, 17.7) * mm});
            skArc(sketch, "E305", {"start": v(441.05, 17.7) * mm, "mid": v(441.69, 22.47) * mm, "end": v(441.05, 27.25) * mm});
            skArc(sketch, "E306", {"start": v(443.8, 39.33) * mm, "mid": v(441.9, 33.4) * mm, "end": v(441.05, 27.25) * mm});
            skArc(sketch, "E307", {"start": v(445.1, 39.54) * mm, "mid": v(456.52, 27.83) * mm, "end": v(469.48, 37.8) * mm});
            skArc(sketch, "E308", {"start": v(469.48, 37.8) * mm, "mid": v(470.08, 41.79) * mm, "end": v(469.48, 45.76) * mm});
            skArc(sketch, "E309", {"start": v(472.74, 61.32) * mm, "mid": v(469.76, 53.82) * mm, "end": v(469.48, 45.76) * mm});
            skArc(sketch, "E310", {"start": v(449.95, 52.35) * mm, "mid": v(458.3, 58.7) * mm, "end": v(463.84, 67.61) * mm});
            skArc(sketch, "E311", {"start": v(418.24, 38.39) * mm, "mid": v(412.88, 34.1) * mm, "end": v(409.06, 28.4) * mm});
            skArc(sketch, "E312", {"start": v(408.55, 46.7) * mm, "mid": v(406.28, 37.73) * mm, "end": v(406.81, 28.48) * mm});
            skArc(sketch, "E313", {"start": v(418.24, 38.39) * mm, "mid": v(425.9, 48.74) * mm, "end": v(432.33, 59.91) * mm});
            skArc(sketch, "E314", {"start": v(382.93, 40.4) * mm, "mid": v(376.88, 35.59) * mm, "end": v(373.45, 28.65) * mm});
            skArc(sketch, "E315", {"start": v(373, 57.36) * mm, "mid": v(371.21, 43.38) * mm, "end": v(371.26, 29.3) * mm});
            skArc(sketch, "E316", {"start": v(382.93, 40.4) * mm, "mid": v(388.27, 48.8) * mm, "end": v(392.86, 57.64) * mm});
            skArc(sketch, "E317", {"start": v(344.19, 37.68) * mm, "mid": v(339.64, 31.9) * mm, "end": v(336.44, 25.28) * mm});
            skArc(sketch, "E318", {"start": v(344.19, 37.68) * mm, "mid": v(349.14, 48.11) * mm, "end": v(353.49, 58.82) * mm});
            skArc(sketch, "E319", {"start": v(327.6, 57.64) * mm, "mid": v(328.8, 42.19) * mm, "end": v(333.89, 27.56) * mm});
            skArc(sketch, "E320", {"start": v(303.17, 35.76) * mm, "mid": v(299.89, 31.03) * mm, "end": v(297.43, 25.83) * mm});
            skArc(sketch, "E321", {"start": v(303.17, 35.76) * mm, "mid": v(305.8, 47.7) * mm, "end": v(306.55, 59.91) * mm});
            skArc(sketch, "E322", {"start": v(295.34, 26.56) * mm, "mid": v(293.53, 30.71) * mm, "end": v(291.32, 34.67) * mm});
            skArc(sketch, "E323", {"start": v(283.3, 53.72) * mm, "mid": v(286.56, 43.87) * mm, "end": v(291.32, 34.67) * mm});
            skArc(sketch, "E324", {"start": v(260.24, 25.74) * mm, "mid": v(262.08, 38.76) * mm, "end": v(262.7, 51.9) * mm});
            skArc(sketch, "E325", {"start": v(257.42, 28.1) * mm, "mid": v(252.7, 35.55) * mm, "end": v(246.66, 41.96) * mm});
            skArc(sketch, "E326", {"start": v(237.91, 60.1) * mm, "mid": v(241.4, 50.6) * mm, "end": v(246.66, 41.96) * mm});
            skArc(sketch, "E327", {"start": v(224.6, 28.38) * mm, "mid": v(225.2, 33.01) * mm, "end": v(225.43, 37.68) * mm});
            skArc(sketch, "E328", {"start": v(225.43, 37.68) * mm, "mid": v(223.62, 46.06) * mm, "end": v(221.14, 54.26) * mm});
            skArc(sketch, "E329", {"start": v(222.15, 30.75) * mm, "mid": v(219.44, 35.1) * mm, "end": v(215.67, 38.59) * mm});
            skArc(sketch, "E330", {"start": v(204.1, 55.72) * mm, "mid": v(209.5, 46.9) * mm, "end": v(215.67, 38.59) * mm});
            skArc(sketch, "E331", {"start": v(165.54, 52.34) * mm, "mid": v(164.12, 57.83) * mm, "end": v(161.68, 62.96) * mm});
            skArc(sketch, "E332", {"start": v(542.3, 170.3) * mm, "mid": v(545.52, 181.72) * mm, "end": v(540.8, 192.6) * mm});
            skArc(sketch, "E333", {"start": v(533.22, 165.98) * mm, "mid": v(538.19, 167.25) * mm, "end": v(542.3, 170.3) * mm});
            skArc(sketch, "E334", {"start": v(533.22, 165.98) * mm, "mid": v(526.7, 160.31) * mm, "end": v(521.75, 153.22) * mm});
            skArc(sketch, "E335", {"start": v(510.29, 156.68) * mm, "mid": v(512.96, 163.27) * mm, "end": v(513.96, 170.3) * mm});
            skArc(sketch, "E336", {"start": v(512.23, 180.37) * mm, "mid": v(512.58, 175.25) * mm, "end": v(513.96, 170.3) * mm});
            skArc(sketch, "E337", {"start": v(522.51, 181.8) * mm, "mid": v(529.37, 177.62) * mm, "end": v(537.22, 179.3) * mm});
            skArc(sketch, "E338", {"start": v(524.67, 196.05) * mm, "mid": v(521.26, 195.51) * mm, "end": v(518.4, 193.57) * mm});
            skArc(sketch, "E339", {"start": v(547.73, 220.1) * mm, "mid": v(550.83, 236.34) * mm, "end": v(543.95, 251.36) * mm});
            skArc(sketch, "E340", {"start": v(535.02, 211.87) * mm, "mid": v(542.17, 214.75) * mm, "end": v(547.73, 220.1) * mm});
            skArc(sketch, "E341", {"start": v(535.02, 211.87) * mm, "mid": v(526.1, 204.32) * mm, "end": v(518.36, 195.55) * mm});
            skArc(sketch, "E342", {"start": v(516.99, 233.5) * mm, "mid": v(527.64, 228.28) * mm, "end": v(539.31, 230.41) * mm});
            skArc(sketch, "E343", {"start": v(505.48, 237.45) * mm, "mid": v(503.58, 228.8) * mm, "end": v(505.31, 220.1) * mm});
            skArc(sketch, "E344", {"start": v(503.76, 203.8) * mm, "mid": v(505.52, 211.86) * mm, "end": v(505.31, 220.1) * mm});
            skArc(sketch, "E345", {"start": v(504.1, 238.83) * mm, "mid": v(493.98, 231.09) * mm, "end": v(484.7, 222.34) * mm});
            skArc(sketch, "E346", {"start": v(517.5, 254.8) * mm, "mid": v(513.99, 251.58) * mm, "end": v(511.15, 247.76) * mm});
            skArc(sketch, "E347", {"start": v(508.92, 248.44) * mm, "mid": v(506.58, 260.07) * mm, "end": v(499.47, 269.56) * mm});
            skArc(sketch, "E348", {"start": v(472.86, 251.2) * mm, "mid": v(484.64, 246.54) * mm, "end": v(497.07, 248.96) * mm});
            skArc(sketch, "E349", {"start": v(473.71, 271.11) * mm, "mid": v(464.55, 262.61) * mm, "end": v(459.46, 251.2) * mm});
            skArc(sketch, "E350", {"start": v(462.72, 225.95) * mm, "mid": v(462.14, 238.7) * mm, "end": v(459.46, 251.2) * mm});
            skArc(sketch, "E351", {"start": v(478, 271.45) * mm, "mid": v(484.76, 279.24) * mm, "end": v(487.62, 289.14) * mm});
            skArc(sketch, "E352", {"start": v(489.34, 290) * mm, "mid": v(502.6, 286.23) * mm, "end": v(510.46, 297.56) * mm});
            skArc(sketch, "E353", {"start": v(514.07, 281.59) * mm, "mid": v(509.7, 268.43) * mm, "end": v(516.47, 256.34) * mm});
            skArc(sketch, "E354", {"start": v(523.17, 253.94) * mm, "mid": v(537.24, 257.52) * mm, "end": v(540.68, 271.63) * mm});
            skArc(sketch, "E355", {"start": v(542.4, 272.48) * mm, "mid": v(555.06, 273) * mm, "end": v(561.63, 283.82) * mm});
            skArc(sketch, "E356", {"start": v(561.63, 283.82) * mm, "mid": v(560.88, 288.52) * mm, "end": v(558.37, 292.58) * mm});
            skArc(sketch, "E357", {"start": v(556.7, 311.62) * mm, "mid": v(556.68, 302.02) * mm, "end": v(558.37, 292.58) * mm});
            skArc(sketch, "E358", {"start": v(538.28, 294.64) * mm, "mid": v(540.94, 304.38) * mm, "end": v(542.45, 314.37) * mm});
            skArc(sketch, "E359", {"start": v(538.28, 294.64) * mm, "mid": v(536, 290.3) * mm, "end": v(534.85, 285.53) * mm});
            skArc(sketch, "E360", {"start": v(532.32, 291.07) * mm, "mid": v(532.54, 287.4) * mm, "end": v(533.3, 283.82) * mm});
            skArc(sketch, "E361", {"start": v(514.07, 281.59) * mm, "mid": v(515.47, 286.23) * mm, "end": v(515.27, 291.07) * mm});
            skArc(sketch, "E362", {"start": v(510.46, 297.56) * mm, "mid": v(509.3, 304.34) * mm, "end": v(504.28, 309.06) * mm});
            skArc(sketch, "E363", {"start": v(499.82, 323.83) * mm, "mid": v(501.9, 316.4) * mm, "end": v(504.28, 309.06) * mm});
            skArc(sketch, "E364", {"start": v(499.82, 323.83) * mm, "mid": v(507.54, 322.67) * mm, "end": v(515.27, 323.83) * mm});
            skArc(sketch, "E365", {"start": v(445.44, 225.28) * mm, "mid": v(448.46, 220.13) * mm, "end": v(454.2, 218.47) * mm});
            skArc(sketch, "E366", {"start": v(451.38, 233.18) * mm, "mid": v(442.4, 230.26) * mm, "end": v(438.62, 221.6) * mm});
            skArc(sketch, "E367", {"start": v(436.13, 210.68) * mm, "mid": v(438.1, 215.98) * mm, "end": v(438.62, 221.6) * mm});
            skArc(sketch, "E368", {"start": v(452.8, 211) * mm, "mid": v(447.77, 209.88) * mm, "end": v(444.35, 206.03) * mm});
            skArc(sketch, "E369", {"start": v(452.8, 211) * mm, "mid": v(455.7, 212.08) * mm, "end": v(458.1, 214.03) * mm});
            skArc(sketch, "E370", {"start": v(484.7, 222.34) * mm, "mid": v(479.57, 214.72) * mm, "end": v(475.27, 206.6) * mm});
            skArc(sketch, "E371", {"start": v(399.32, 114.34) * mm, "mid": v(408.77, 116.65) * mm, "end": v(414.45, 124.56) * mm});
            skArc(sketch, "E372", {"start": v(414.45, 124.56) * mm, "mid": v(414.5, 128.07) * mm, "end": v(413.16, 131.3) * mm});
            skArc(sketch, "E373", {"start": v(417.1, 143.23) * mm, "mid": v(414.71, 137.4) * mm, "end": v(413.16, 131.3) * mm});
            skArc(sketch, "E374", {"start": v(405.73, 123.4) * mm, "mid": v(402.98, 129.03) * mm, "end": v(397.14, 131.3) * mm});
            skArc(sketch, "E375", {"start": v(402.32, 140.98) * mm, "mid": v(396.83, 139.91) * mm, "end": v(392.03, 137.03) * mm});
            skArc(sketch, "E376", {"start": v(402.32, 140.98) * mm, "mid": v(406.27, 145.5) * mm, "end": v(409.2, 150.73) * mm});
            skArc(sketch, "E377", {"start": v(328.51, 96.82) * mm, "mid": v(336.7, 90.8) * mm, "end": v(343.98, 97.9) * mm});
            skArc(sketch, "E378", {"start": v(343.98, 97.9) * mm, "mid": v(344.3, 101.2) * mm, "end": v(343.98, 104.5) * mm});
            skArc(sketch, "E379", {"start": v(332.51, 108.62) * mm, "mid": v(330.75, 106.79) * mm, "end": v(329.27, 104.72) * mm});
            skArc(sketch, "E380", {"start": v(332.51, 108.62) * mm, "mid": v(335.24, 112.6) * mm, "end": v(337.38, 116.95) * mm});
            skArc(sketch, "E381", {"start": v(347.47, 116.78) * mm, "mid": v(345.28, 110.77) * mm, "end": v(343.98, 104.5) * mm});
            skArc(sketch, "E382", {"start": v(291.48, 88.03) * mm, "mid": v(298.04, 81.45) * mm, "end": v(306.42, 85.46) * mm});
            skArc(sketch, "E383", {"start": v(292.17, 95.33) * mm, "mid": v(291.47, 91.71) * mm, "end": v(291.48, 88.03) * mm});
            skArc(sketch, "E384", {"start": v(292.17, 95.33) * mm, "mid": v(291.34, 100.36) * mm, "end": v(290.02, 105.29) * mm});
            skArc(sketch, "E385", {"start": v(299.34, 106.88) * mm, "mid": v(302.5, 100.37) * mm, "end": v(306.64, 94.43) * mm});
            skArc(sketch, "E386", {"start": v(257.22, 185.89) * mm, "mid": v(259.33, 182.9) * mm, "end": v(262.54, 181.17) * mm});
            skArc(sketch, "E387", {"start": v(268.38, 174.21) * mm, "mid": v(265.94, 178.09) * mm, "end": v(262.54, 181.17) * mm});
            skArc(sketch, "E388", {"start": v(277.4, 187.52) * mm, "mid": v(276.58, 180.88) * mm, "end": v(277.83, 174.3) * mm});
            skArc(sketch, "E389", {"start": v(277.4, 187.52) * mm, "mid": v(278.27, 191.21) * mm, "end": v(277.4, 194.9) * mm});
            skArc(sketch, "E390", {"start": v(277.4, 194.9) * mm, "mid": v(272.83, 200.46) * mm, "end": v(266.23, 203.32) * mm});
            skArc(sketch, "E391", {"start": v(263.31, 187.52) * mm, "mid": v(268.5, 189.34) * mm, "end": v(272.24, 193.36) * mm});
            skArc(sketch, "E392", {"start": v(256.79, 197.4) * mm, "mid": v(255.84, 195.22) * mm, "end": v(255.76, 192.84) * mm});
            skArc(sketch, "E393", {"start": v(285.82, 204.14) * mm, "mid": v(291.77, 198.29) * mm, "end": v(299.88, 196.35) * mm});
            skArc(sketch, "E394", {"start": v(302.37, 212.36) * mm, "mid": v(296.87, 210.56) * mm, "end": v(293.5, 205.87) * mm});
            skArc(sketch, "E395", {"start": v(308.64, 214.52) * mm, "mid": v(306.06, 219.05) * mm, "end": v(301.5, 221.6) * mm});
            skArc(sketch, "E396", {"start": v(286.57, 214.85) * mm, "mid": v(284.53, 209.6) * mm, "end": v(285.82, 204.14) * mm});
            skArc(sketch, "E397", {"start": v(294.47, 229.99) * mm, "mid": v(297.06, 225.02) * mm, "end": v(301.5, 221.6) * mm});
            skArc(sketch, "E398", {"start": v(286.57, 214.85) * mm, "mid": v(286.18, 221.62) * mm, "end": v(283.44, 227.83) * mm});
            skArc(sketch, "E399", {"start": v(243.95, 286.15) * mm, "mid": v(246.73, 292.3) * mm, "end": v(247.98, 298.93) * mm});
            skArc(sketch, "E400", {"start": v(243.95, 286.15) * mm, "mid": v(240.64, 269.6) * mm, "end": v(242.55, 252.83) * mm});
            skArc(sketch, "E401", {"start": v(223.5, 249.91) * mm, "mid": v(216.44, 264.67) * mm, "end": v(205.45, 276.8) * mm});
            skArc(sketch, "E402", {"start": v(205.45, 223.1) * mm, "mid": v(199.92, 228.66) * mm, "end": v(192.4, 230.9) * mm});
            skArc(sketch, "E403", {"start": v(190.43, 215.36) * mm, "mid": v(195.37, 217.1) * mm, "end": v(197.98, 221.63) * mm});
            skArc(sketch, "E404", {"start": v(204.96, 213.3) * mm, "mid": v(205.85, 218.17) * mm, "end": v(205.45, 223.1) * mm});
            skArc(sketch, "E405", {"start": v(204.96, 213.3) * mm, "mid": v(206.56, 208.44) * mm, "end": v(208.48, 203.69) * mm});
            skArc(sketch, "E406", {"start": v(198.86, 199.95) * mm, "mid": v(196.23, 204.56) * mm, "end": v(192.16, 207.98) * mm});
            skArc(sketch, "E407", {"start": v(185, 212.49) * mm, "mid": v(188.15, 209.54) * mm, "end": v(192.16, 207.98) * mm});
            skArc(sketch, "E408", {"start": v(183.99, 223.1) * mm, "mid": v(183.08, 221.63) * mm, "end": v(182.5, 220.02) * mm});
            skArc(sketch, "E409", {"start": v(178.18, 230.05) * mm, "mid": v(179.7, 224.76) * mm, "end": v(182.5, 220.02) * mm});
            skArc(sketch, "E410", {"start": v(247.98, 131.3) * mm, "mid": v(245.23, 133.29) * mm, "end": v(242.05, 134.45) * mm});
            skArc(sketch, "E411", {"start": v(242.05, 126.77) * mm, "mid": v(237.99, 124.59) * mm, "end": v(235.34, 120.82) * mm});
            skArc(sketch, "E412", {"start": v(237.18, 140.98) * mm, "mid": v(239.54, 137.66) * mm, "end": v(242.05, 134.45) * mm});
            skArc(sketch, "E413", {"start": v(229.17, 125.47) * mm, "mid": v(229.3, 132.05) * mm, "end": v(227.34, 138.34) * mm});
            skArc(sketch, "E414", {"start": v(229.17, 125.47) * mm, "mid": v(229.44, 119.53) * mm, "end": v(233.6, 115.3) * mm});
            skArc(sketch, "E415", {"start": v(233.6, 115.3) * mm, "mid": v(237.57, 113.18) * mm, "end": v(242.05, 112.92) * mm});
            skLineSegment(sketch, "E416", {"start": v(119.84, 198.51) * mm, "end": v(116.86, 208.85) * mm});
            skLineSegment(sketch, "E417", {"start": v(104.57, 203.45) * mm, "end": v(112.95, 191.74) * mm});
            skLineSegment(sketch, "E418", {"start": v(101.01, 182.9) * mm, "end": v(92.05, 193) * mm});
            skLineSegment(sketch, "E419", {"start": v(125.93, 186) * mm, "end": v(126.8, 186.39) * mm});
            skLineSegment(sketch, "E420", {"start": v(126.8, 186.39) * mm, "end": v(184.01, 56.61) * mm});
            skLineSegment(sketch, "E421", {"start": v(184.01, 56.61) * mm, "end": v(182.65, 55.67) * mm});
            skLineSegment(sketch, "E422", {"start": v(173.62, 67.73) * mm, "end": v(129.84, 162.91) * mm});
            skLineSegment(sketch, "E423", {"start": v(115.37, 157.63) * mm, "end": v(161.68, 62.96) * mm});
            skLineSegment(sketch, "E424", {"start": v(204.1, 55.72) * mm, "end": v(132.7, 217) * mm});
            skLineSegment(sketch, "E425", {"start": v(161.07, 221.55) * mm, "end": v(221.14, 54.26) * mm});
            skLineSegment(sketch, "E426", {"start": v(237.91, 60.1) * mm, "end": v(185, 212.49) * mm});
            skLineSegment(sketch, "E427", {"start": v(198.86, 199.95) * mm, "end": v(227.34, 138.34) * mm});
            skLineSegment(sketch, "E428", {"start": v(237.18, 140.98) * mm, "end": v(208.48, 203.69) * mm});
            skLineSegment(sketch, "E429", {"start": v(262.7, 51.9) * mm, "end": v(250.66, 119.11) * mm});
            skLineSegment(sketch, "E430", {"start": v(250.66, 119.11) * mm, "end": v(248.93, 119) * mm});
            skLineSegment(sketch, "E431", {"start": v(248.93, 119) * mm, "end": v(242.05, 126.77) * mm});
            skLineSegment(sketch, "E432", {"start": v(242.05, 112.92) * mm, "end": v(235.34, 120.82) * mm});
            skLineSegment(sketch, "E433", {"start": v(247.98, 131.3) * mm, "end": v(223.5, 249.91) * mm});
            skLineSegment(sketch, "E434", {"start": v(190.43, 215.36) * mm, "end": v(183.99, 223.1) * mm});
            skLineSegment(sketch, "E435", {"start": v(197.98, 221.63) * mm, "end": v(192.4, 230.9) * mm});
            skLineSegment(sketch, "E436", {"start": v(242.55, 252.83) * mm, "end": v(255.76, 192.84) * mm});
            skLineSegment(sketch, "E437", {"start": v(257.22, 185.89) * mm, "end": v(283.3, 53.72) * mm});
            skLineSegment(sketch, "E438", {"start": v(306.55, 59.91) * mm, "end": v(306.42, 85.46) * mm});
            skLineSegment(sketch, "E439", {"start": v(290.02, 105.29) * mm, "end": v(268.38, 174.21) * mm});
            skLineSegment(sketch, "E440", {"start": v(277.83, 174.3) * mm, "end": v(299.34, 106.88) * mm});
            skLineSegment(sketch, "E441", {"start": v(306.64, 94.43) * mm, "end": v(309.03, 203.45) * mm});
            skLineSegment(sketch, "E442", {"start": v(309.03, 203.45) * mm, "end": v(302.37, 212.36) * mm});
            skLineSegment(sketch, "E443", {"start": v(299.88, 196.35) * mm, "end": v(293.5, 205.87) * mm});
            skLineSegment(sketch, "E444", {"start": v(256.79, 197.4) * mm, "end": v(263.31, 187.52) * mm});
            skLineSegment(sketch, "E445", {"start": v(272.24, 193.36) * mm, "end": v(266.23, 203.32) * mm});
            skLineSegment(sketch, "E446", {"start": v(283.44, 227.83) * mm, "end": v(259.34, 286.92) * mm});
            skLineSegment(sketch, "E447", {"start": v(294.47, 229.99) * mm, "end": v(279.6, 264.35) * mm});
            skLineSegment(sketch, "E448", {"start": v(276.27, 277.08) * mm, "end": v(268.46, 290.82) * mm});
            skLineSegment(sketch, "E449", {"start": v(308.64, 214.52) * mm, "end": v(310.85, 274.47) * mm});
            skLineSegment(sketch, "E450", {"start": v(332.75, 272.1) * mm, "end": v(331.04, 219.18) * mm});
            skLineSegment(sketch, "E451", {"start": v(339.72, 220.19) * mm, "end": v(331.9, 211.18) * mm});
            skLineSegment(sketch, "E452", {"start": v(331.9, 211.18) * mm, "end": v(331.04, 211.35) * mm});
            skLineSegment(sketch, "E453", {"start": v(331.04, 211.35) * mm, "end": v(329.27, 104.72) * mm});
            skLineSegment(sketch, "E454", {"start": v(337.38, 116.95) * mm, "end": v(361.76, 180.5) * mm});
            skLineSegment(sketch, "E455", {"start": v(370.06, 175.3) * mm, "end": v(347.47, 116.78) * mm});
            skLineSegment(sketch, "E456", {"start": v(328.51, 96.82) * mm, "end": v(327.6, 57.64) * mm});
            skLineSegment(sketch, "E457", {"start": v(353.49, 58.82) * mm, "end": v(382.09, 190.61) * mm});
            skLineSegment(sketch, "E458", {"start": v(370.15, 207.75) * mm, "end": v(369.15, 198.9) * mm});
            skLineSegment(sketch, "E459", {"start": v(378.53, 197.36) * mm, "end": v(379.54, 206.93) * mm});
            skLineSegment(sketch, "E460", {"start": v(351.15, 212.66) * mm, "end": v(344.06, 202.97) * mm});
            skLineSegment(sketch, "E461", {"start": v(373, 57.36) * mm, "end": v(387.2, 122.83) * mm});
            skLineSegment(sketch, "E462", {"start": v(387.2, 122.83) * mm, "end": v(389.79, 122.71) * mm});
            skLineSegment(sketch, "E463", {"start": v(389.79, 122.71) * mm, "end": v(397.14, 131.3) * mm});
            skLineSegment(sketch, "E464", {"start": v(405.73, 123.4) * mm, "end": v(399.32, 114.34) * mm});
            skLineSegment(sketch, "E465", {"start": v(392.86, 57.64) * mm, "end": v(458.1, 214.03) * mm});
            skLineSegment(sketch, "E466", {"start": v(444.35, 206.03) * mm, "end": v(417.1, 143.23) * mm});
            skLineSegment(sketch, "E467", {"start": v(409.2, 150.73) * mm, "end": v(436.13, 210.68) * mm});
            skLineSegment(sketch, "E468", {"start": v(451.38, 233.18) * mm, "end": v(445.44, 225.28) * mm});
            skLineSegment(sketch, "E469", {"start": v(454.2, 218.47) * mm, "end": v(460.31, 225.28) * mm});
            skLineSegment(sketch, "E470", {"start": v(460.31, 225.28) * mm, "end": v(462.72, 225.95) * mm});
            skLineSegment(sketch, "E471", {"start": v(475.27, 206.6) * mm, "end": v(408.55, 46.7) * mm});
            skLineSegment(sketch, "E472", {"start": v(432.33, 59.91) * mm, "end": v(503.76, 203.8) * mm});
            skLineSegment(sketch, "E473", {"start": v(512.23, 180.37) * mm, "end": v(449.95, 52.35) * mm});
            skLineSegment(sketch, "E474", {"start": v(463.84, 67.61) * mm, "end": v(510.29, 156.68) * mm});
            skLineSegment(sketch, "E475", {"start": v(521.75, 153.22) * mm, "end": v(472.74, 61.32) * mm});
            skLineSegment(sketch, "E476", {"start": v(518.4, 193.57) * mm, "end": v(518.36, 195.55) * mm});
            skLineSegment(sketch, "E477", {"start": v(524.67, 196.05) * mm, "end": v(522.51, 181.8) * mm});
            skLineSegment(sketch, "E478", {"start": v(537.33, 179.5) * mm, "end": v(540.8, 192.6) * mm});
            skLineSegment(sketch, "E479", {"start": v(539.31, 230.41) * mm, "end": v(543.95, 251.36) * mm});
            skLineSegment(sketch, "E480", {"start": v(516.99, 233.5) * mm, "end": v(523.17, 253.94) * mm});
            skLineSegment(sketch, "E481", {"start": v(511.15, 247.76) * mm, "end": v(508.92, 248.44) * mm});
            skLineSegment(sketch, "E482", {"start": v(505.48, 237.45) * mm, "end": v(504.1, 238.83) * mm});
            skLineSegment(sketch, "E483", {"start": v(516.47, 256.34) * mm, "end": v(517.5, 254.8) * mm});
            skLineSegment(sketch, "E484", {"start": v(499.47, 269.56) * mm, "end": v(497.07, 248.96) * mm});
            skLineSegment(sketch, "E485", {"start": v(472.86, 251.2) * mm, "end": v(478, 271.45) * mm});
            skLineSegment(sketch, "E486", {"start": v(540.68, 271.63) * mm, "end": v(542.4, 272.48) * mm});
            skLineSegment(sketch, "E487", {"start": v(534.85, 285.53) * mm, "end": v(533.3, 283.82) * mm});
            skLineSegment(sketch, "E488", {"start": v(473.71, 271.11) * mm, "end": v(477.47, 285.72) * mm});
            skLineSegment(sketch, "E489", {"start": v(487.62, 289.14) * mm, "end": v(489.34, 290) * mm});
            skLineSegment(sketch, "E490", {"start": v(515.27, 291.07) * mm, "end": v(515.27, 323.83) * mm});
            skArc(sketch, "E491", {"start": v(510.43, 365.53) * mm, "mid": v(512.02, 358.94) * mm, "end": v(515.43, 353.09) * mm});
            skArc(sketch, "E492", {"start": v(494.85, 353.19) * mm, "mid": v(497.25, 357.93) * mm, "end": v(497.77, 363.22) * mm});
            skArc(sketch, "E493", {"start": v(293.49, 306.6) * mm, "mid": v(294.86, 306.28) * mm, "end": v(296.24, 306.6) * mm});
            skArc(sketch, "E494", {"start": v(293.12, 324.7) * mm, "mid": v(293.53, 322.39) * mm, "end": v(294.36, 320.2) * mm});
            skLineSegment(sketch, "E495", {"start": v(279.74, 306.6) * mm, "end": v(278.3, 328.22) * mm});
            skLineSegment(sketch, "E496", {"start": v(306.8, 314.26) * mm, "end": v(303.54, 337.46) * mm});
            skLineSegment(sketch, "E497", {"start": v(333.7, 318.6) * mm, "end": v(329.78, 339.38) * mm});
            skLineSegment(sketch, "E498", {"start": v(329.78, 339.38) * mm, "end": v(327.58, 340.13) * mm});
            skLineSegment(sketch, "E499", {"start": v(276.81, 328) * mm, "end": v(272.6, 333.78) * mm});
            skLineSegment(sketch, "E500", {"start": v(271.83, 323.36) * mm, "end": v(267.53, 330.67) * mm});
            skLineSegment(sketch, "E501", {"start": v(277.52, 334.72) * mm, "end": v(271.56, 410.5) * mm});
            skLineSegment(sketch, "E502", {"start": v(251.74, 400.2) * mm, "end": v(269.49, 345.79) * mm});
            skLineSegment(sketch, "E503", {"start": v(263.58, 343.27) * mm, "end": v(245.43, 397.1) * mm});
            skLineSegment(sketch, "E504", {"start": v(247.96, 448.24) * mm, "end": v(240.21, 411.78) * mm});
            skLineSegment(sketch, "E505", {"start": v(234.57, 446.65) * mm, "end": v(214.64, 359.24) * mm});
            skLineSegment(sketch, "E506", {"start": v(225.78, 355.68) * mm, "end": v(238.48, 406.93) * mm});
            skLineSegment(sketch, "E507", {"start": v(247.62, 308.48) * mm, "end": v(253.56, 300.73) * mm});
            skLineSegment(sketch, "E508", {"start": v(256.01, 314.7) * mm, "end": v(261.15, 306.6) * mm});
            skLineSegment(sketch, "E509", {"start": v(220.95, 321.92) * mm, "end": v(232.01, 301.25) * mm});
            skLineSegment(sketch, "E510", {"start": v(210.16, 290.11) * mm, "end": v(199.46, 312.16) * mm});
            skArc(sketch, "E511", {"start": v(199.46, 312.16) * mm, "mid": v(202.58, 316.96) * mm, "end": v(205, 322.15) * mm});
            skLineSegment(sketch, "E512", {"start": v(196.5, 307.87) * mm, "end": v(195.49, 309.28) * mm});
            skLineSegment(sketch, "E513", {"start": v(188.9, 304.36) * mm, "end": v(193.75, 319.33) * mm});
            skLineSegment(sketch, "E514", {"start": v(169.52, 312.75) * mm, "end": v(175.67, 327.07) * mm});
            skLineSegment(sketch, "E515", {"start": v(199.14, 358.87) * mm, "end": v(219.36, 482.42) * mm});
            skLineSegment(sketch, "E516", {"start": v(204.08, 481.56) * mm, "end": v(193.43, 417.5) * mm});
            skLineSegment(sketch, "E517", {"start": v(171.8, 461.47) * mm, "end": v(164.58, 430.39) * mm});
            skLineSegment(sketch, "E518", {"start": v(160.97, 465.25) * mm, "end": v(137.1, 370.8) * mm});
            skLineSegment(sketch, "E519", {"start": v(148.78, 366.68) * mm, "end": v(160.12, 415.1) * mm});
            skLineSegment(sketch, "E520", {"start": v(165.95, 397.6) * mm, "end": v(150.5, 349.34) * mm});
            skLineSegment(sketch, "E521", {"start": v(176.26, 393.81) * mm, "end": v(153.84, 319.85) * mm});
            skLineSegment(sketch, "E522", {"start": v(142.35, 321.12) * mm, "end": v(146.03, 338.7) * mm});
            skLineSegment(sketch, "E523", {"start": v(123.98, 323.56) * mm, "end": v(126.4, 342.02) * mm});
            skLineSegment(sketch, "E524", {"start": v(106.64, 326.9) * mm, "end": v(115.29, 465.39) * mm});
            skLineSegment(sketch, "E525", {"start": v(132.3, 462.16) * mm, "end": v(126.12, 358.6) * mm});
            skLineSegment(sketch, "E526", {"start": v(99.06, 333.15) * mm, "end": v(97.76, 436.3) * mm});
            skLineSegment(sketch, "E527", {"start": v(85.21, 436.72) * mm, "end": v(86.54, 331.95) * mm});
            skLineSegment(sketch, "E528", {"start": v(184, 357.5) * mm, "end": v(190.98, 406.09) * mm});
            skArc(sketch, "E529", {"start": v(188.12, 406.77) * mm, "mid": v(181.5, 400.93) * mm, "end": v(176.26, 393.81) * mm});
            skArc(sketch, "E530", {"start": v(165.95, 397.6) * mm, "mid": v(164.98, 403.9) * mm, "end": v(163.72, 410.18) * mm});
            skArc(sketch, "E531", {"start": v(160.12, 415.1) * mm, "mid": v(161.8, 412.56) * mm, "end": v(163.72, 410.18) * mm});
            skArc(sketch, "E532", {"start": v(190.98, 406.09) * mm, "mid": v(189.67, 406.93) * mm, "end": v(188.12, 406.77) * mm});
            skArc(sketch, "E533", {"start": v(148.78, 366.68) * mm, "mid": v(147.74, 358.02) * mm, "end": v(148.61, 349.34) * mm});
            skArc(sketch, "E534", {"start": v(148.61, 349.34) * mm, "mid": v(149.56, 348.65) * mm, "end": v(150.5, 349.34) * mm});
            skArc(sketch, "E535", {"start": v(127.49, 354.42) * mm, "mid": v(133.97, 361.63) * mm, "end": v(137.1, 370.8) * mm});
            skArc(sketch, "E536", {"start": v(126.12, 358.6) * mm, "mid": v(126.4, 356.38) * mm, "end": v(127.49, 354.42) * mm});
            skArc(sketch, "E537", {"start": v(125.01, 294.29) * mm, "mid": v(125.97, 294.03) * mm, "end": v(126.85, 294.47) * mm});
            skArc(sketch, "E538", {"start": v(131.1, 283.68) * mm, "mid": v(129.78, 284.29) * mm, "end": v(128.46, 283.68) * mm});
            skArc(sketch, "E539", {"start": v(101.36, 292.52) * mm, "mid": v(101.3, 294) * mm, "end": v(101.01, 295.43) * mm});
            skArc(sketch, "E540", {"start": v(102.84, 456.5) * mm, "mid": v(98.99, 446.73) * mm, "end": v(97.76, 436.3) * mm});
            skArc(sketch, "E541", {"start": v(85.21, 436.72) * mm, "mid": v(84.03, 445.46) * mm, "end": v(80.76, 453.64) * mm});
            skArc(sketch, "E542", {"start": v(74.47, 463.93) * mm, "mid": v(76.39, 458.04) * mm, "end": v(80.76, 453.64) * mm});
            skArc(sketch, "E543", {"start": v(78.69, 482.64) * mm, "mid": v(74.79, 473.7) * mm, "end": v(74.47, 463.93) * mm});
            skArc(sketch, "E544", {"start": v(82.58, 466.53) * mm, "mid": v(90.73, 466.42) * mm, "end": v(97.76, 470.53) * mm});
            skArc(sketch, "E545", {"start": v(102.84, 456.5) * mm, "mid": v(105.53, 462.59) * mm, "end": v(105.95, 469.23) * mm});
            skArc(sketch, "E546", {"start": v(105.95, 469.23) * mm, "mid": v(101.67, 479.45) * mm, "end": v(93.72, 487.19) * mm});
            skArc(sketch, "E547", {"start": v(115.29, 465.39) * mm, "mid": v(113.4, 474.03) * mm, "end": v(107.25, 480.37) * mm});
            skArc(sketch, "E548", {"start": v(137.97, 479.07) * mm, "mid": v(134.01, 471) * mm, "end": v(132.3, 462.16) * mm});
            skArc(sketch, "E549", {"start": v(137.97, 479.07) * mm, "mid": v(142.56, 485.3) * mm, "end": v(143.8, 492.92) * mm});
            skArc(sketch, "E550", {"start": v(160.97, 465.25) * mm, "mid": v(161.13, 474.56) * mm, "end": v(157.12, 482.97) * mm});
            skArc(sketch, "E551", {"start": v(182, 477.13) * mm, "mid": v(175.51, 470.2) * mm, "end": v(171.8, 461.47) * mm});
            skArc(sketch, "E552", {"start": v(182, 477.13) * mm, "mid": v(185.48, 482.4) * mm, "end": v(185.9, 488.7) * mm});
            skLineSegment(sketch, "E553", {"start": v(133.4, 499.3) * mm, "end": v(125.68, 517.24) * mm});
            skLineSegment(sketch, "E554", {"start": v(114.82, 494.29) * mm, "end": v(108.56, 508.82) * mm});
            skArc(sketch, "E555", {"start": v(143.8, 492.92) * mm, "mid": v(138.69, 508.02) * mm, "end": v(125.68, 517.24) * mm});
            skArc(sketch, "E556", {"start": v(108.56, 508.82) * mm, "mid": v(103.15, 494.82) * mm, "end": v(107.25, 480.37) * mm});
            skArc(sketch, "E557", {"start": v(114.82, 494.29) * mm, "mid": v(124.62, 494.93) * mm, "end": v(133.4, 499.3) * mm});
            skLineSegment(sketch, "E558", {"start": v(180.62, 490.86) * mm, "end": v(183.08, 502.94) * mm});
            skArc(sketch, "E559", {"start": v(185.9, 488.7) * mm, "mid": v(185.11, 495.95) * mm, "end": v(183.08, 502.94) * mm});
            skLineSegment(sketch, "E560", {"start": v(166.17, 492.36) * mm, "end": v(168.7, 504.75) * mm});
            skArc(sketch, "E561", {"start": v(168.7, 504.75) * mm, "mid": v(159.5, 495.67) * mm, "end": v(157.12, 482.97) * mm});
            skLineSegment(sketch, "E562", {"start": v(180.62, 490.86) * mm, "end": v(180.24, 489) * mm});
            skLineSegment(sketch, "E563", {"start": v(166.17, 492.36) * mm, "end": v(165.76, 490.37) * mm});
            skArc(sketch, "E564", {"start": v(165.76, 490.37) * mm, "mid": v(172.83, 487.93) * mm, "end": v(180.24, 489) * mm});
            skPoint(sketch, "E565.orphan", {"position": v(171.23, 517.15) * mm});
            skPoint(sketch, "E566.orphan", {"position": v(185.55, 515.03) * mm});
            skPoint(sketch, "E567.orphan", {"position": v(179.86, 487.13) * mm});
            skPoint(sketch, "E568.orphan", {"position": v(165.36, 488.38) * mm});
            skPoint(sketch, "E569.orphan", {"position": v(102.3, 523.35) * mm});
            skLineSegment(sketch, "E570", {"start": v(78.69, 482.64) * mm, "end": v(82.58, 466.53) * mm});
            skLineSegment(sketch, "E571", {"start": v(97.76, 470.53) * mm, "end": v(93.72, 487.19) * mm});
            skLineSegment(sketch, "E572", {"start": v(169.7, 418.8) * mm, "end": v(170.37, 432.56) * mm});
            skLineSegment(sketch, "E573", {"start": v(183.87, 417.5) * mm, "end": v(184.41, 431.81) * mm});
            skCircle(sketch, "E574.cCircle", {"center": v(213.16, 497.83) * mm, "radius": 9.53 * mm, "construction": true});
            skLineSegment(sketch, "E574.0", {"start": v(209.06, 508.04) * mm, "end": v(219.95, 506.48) * mm});
            skLineSegment(sketch, "E574.1", {"start": v(219.95, 506.48) * mm, "end": v(224.05, 496.27) * mm});
            skLineSegment(sketch, "E574.2", {"start": v(224.05, 496.27) * mm, "end": v(217.26, 487.62) * mm});
            skLineSegment(sketch, "E574.3", {"start": v(217.26, 487.62) * mm, "end": v(206.37, 489.18) * mm});
            skLineSegment(sketch, "E574.4", {"start": v(206.37, 489.18) * mm, "end": v(202.27, 499.38) * mm});
            skLineSegment(sketch, "E574.5", {"start": v(202.27, 499.38) * mm, "end": v(209.06, 508.04) * mm});
            skPoint(sketch, "E574.0.midPoint", {"position": v(214.5, 507.26) * mm});
            skArc(sketch, "E575", {"start": v(225.93, 490.34) * mm, "mid": v(214.08, 512.6) * mm, "end": v(199.56, 491.99) * mm});
            skArc(sketch, "E576", {"start": v(199.56, 491.99) * mm, "mid": v(201.65, 486.7) * mm, "end": v(204.08, 481.56) * mm});
            skArc(sketch, "E577", {"start": v(219.36, 482.42) * mm, "mid": v(223.13, 485.98) * mm, "end": v(225.93, 490.34) * mm});
            skArc(sketch, "E578", {"start": v(169.7, 418.8) * mm, "mid": v(176.56, 415.78) * mm, "end": v(183.87, 417.5) * mm});
            skArc(sketch, "E579", {"start": v(193.43, 417.5) * mm, "mid": v(189.65, 425.12) * mm, "end": v(184.41, 431.81) * mm});
            skArc(sketch, "E580", {"start": v(170.37, 432.56) * mm, "mid": v(167.3, 431.93) * mm, "end": v(164.58, 430.39) * mm});
            skLineSegment(sketch, "E581", {"start": v(96.42, 240.08) * mm, "end": v(94.77, 241.77) * mm});
            skLineSegment(sketch, "E582", {"start": v(94.77, 241.77) * mm, "end": v(85.62, 254.9) * mm});
            skLineSegment(sketch, "E583", {"start": v(114.56, 252.95) * mm, "end": v(103.54, 270.74) * mm});
            skLineSegment(sketch, "E584", {"start": v(115.94, 266.27) * mm, "end": v(116.97, 267.99) * mm});
            skLineSegment(sketch, "E585", {"start": v(125.82, 259.9) * mm, "end": v(128.69, 259.9) * mm});
            skLineSegment(sketch, "E586", {"start": v(125.82, 273.62) * mm, "end": v(127.65, 273.96) * mm});
            skLineSegment(sketch, "E587", {"start": v(142, 261.06) * mm, "end": v(130.83, 277.76) * mm});
            skLineSegment(sketch, "E588", {"start": v(130.83, 277.76) * mm, "end": v(128.23, 278.28) * mm});
            skLineSegment(sketch, "E589", {"start": v(161.87, 273.92) * mm, "end": v(150.74, 288.62) * mm});
            skLineSegment(sketch, "E590", {"start": v(134.08, 249.46) * mm, "end": v(131.44, 248.24) * mm});
            skLineSegment(sketch, "E591", {"start": v(187.93, 42.35) * mm, "end": v(190.03, 41.71) * mm});
            skLineSegment(sketch, "E592", {"start": v(224.6, 28.38) * mm, "end": v(222.15, 30.75) * mm});
            skLineSegment(sketch, "E593", {"start": v(223.3, 16.97) * mm, "end": v(221.42, 17.55) * mm});
            skLineSegment(sketch, "E594", {"start": v(259.62, 13.21) * mm, "end": v(257.3, 13.21) * mm});
            skLineSegment(sketch, "E595", {"start": v(260.24, 25.74) * mm, "end": v(257.42, 28.1) * mm});
            skLineSegment(sketch, "E596", {"start": v(297.38, 13.21) * mm, "end": v(294.78, 13.21) * mm});
            skLineSegment(sketch, "E597", {"start": v(297.43, 25.83) * mm, "end": v(295.34, 26.56) * mm});
            skLineSegment(sketch, "E598", {"start": v(336.6, 10.6) * mm, "end": v(334.28, 10.6) * mm});
            skLineSegment(sketch, "E599", {"start": v(336.44, 25.28) * mm, "end": v(333.89, 27.56) * mm});
            skLineSegment(sketch, "E600", {"start": v(374.64, 14.51) * mm, "end": v(372.62, 13.21) * mm});
            skLineSegment(sketch, "E601", {"start": v(373.45, 28.65) * mm, "end": v(371.26, 29.3) * mm});
            skLineSegment(sketch, "E602", {"start": v(408.79, 18.7) * mm, "end": v(407.05, 19) * mm});
            skLineSegment(sketch, "E603", {"start": v(409.06, 28.4) * mm, "end": v(406.81, 28.48) * mm});
            skLineSegment(sketch, "E604", {"start": v(445.1, 39.54) * mm, "end": v(443.8, 39.33) * mm});
            skLineSegment(sketch, "E605", {"start": v(392.03, 137.03) * mm, "end": v(391.07, 138.2) * mm});
            skCircle(sketch, "E606.cCircle", {"center": v(92.95, 304.98) * mm, "radius": 6.99 * mm, "construction": true});
            skLineSegment(sketch, "E606.0", {"start": v(98.43, 299.06) * mm, "end": v(90.56, 297.27) * mm});
            skLineSegment(sketch, "E606.1", {"start": v(90.56, 297.27) * mm, "end": v(85.08, 303.19) * mm});
            skLineSegment(sketch, "E606.2", {"start": v(85.08, 303.19) * mm, "end": v(87.46, 310.9) * mm});
            skLineSegment(sketch, "E606.3", {"start": v(87.46, 310.9) * mm, "end": v(95.33, 312.69) * mm});
            skLineSegment(sketch, "E606.4", {"start": v(95.33, 312.69) * mm, "end": v(100.81, 306.77) * mm});
            skLineSegment(sketch, "E606.5", {"start": v(100.81, 306.77) * mm, "end": v(98.43, 299.06) * mm});
            skPoint(sketch, "E606.0.midPoint", {"position": v(94.5, 298.16) * mm});
            skCircle(sketch, "E607.cCircle", {"center": v(111.94, 282.63) * mm, "radius": 8.4 * mm, "construction": true});
            skLineSegment(sketch, "E607.0", {"start": v(115.52, 273.6) * mm, "end": v(105.92, 275.02) * mm});
            skLineSegment(sketch, "E607.1", {"start": v(105.92, 275.02) * mm, "end": v(102.34, 284.04) * mm});
            skLineSegment(sketch, "E607.2", {"start": v(102.34, 284.04) * mm, "end": v(108.37, 291.65) * mm});
            skLineSegment(sketch, "E607.3", {"start": v(108.37, 291.65) * mm, "end": v(117.97, 290.23) * mm});
            skLineSegment(sketch, "E607.4", {"start": v(117.97, 290.23) * mm, "end": v(121.54, 281.2) * mm});
            skLineSegment(sketch, "E607.5", {"start": v(121.54, 281.2) * mm, "end": v(115.52, 273.6) * mm});
            skPoint(sketch, "E607.0.midPoint", {"position": v(110.72, 274.31) * mm});
            skCircle(sketch, "E608.cCircle", {"center": v(138.52, 293.12) * mm, "radius": 6.05 * mm, "construction": true});
            skLineSegment(sketch, "E608.0", {"start": v(139.43, 286.2) * mm, "end": v(132.98, 288.87) * mm});
            skLineSegment(sketch, "E608.1", {"start": v(132.98, 288.87) * mm, "end": v(132.07, 295.8) * mm});
            skLineSegment(sketch, "E608.2", {"start": v(132.07, 295.8) * mm, "end": v(137.6, 300.05) * mm});
            skLineSegment(sketch, "E608.3", {"start": v(137.6, 300.05) * mm, "end": v(144.06, 297.37) * mm});
            skLineSegment(sketch, "E608.4", {"start": v(144.06, 297.37) * mm, "end": v(144.97, 290.44) * mm});
            skLineSegment(sketch, "E608.5", {"start": v(144.97, 290.44) * mm, "end": v(139.43, 286.2) * mm});
            skPoint(sketch, "E608.0.midPoint", {"position": v(136.2, 287.53) * mm});
            skCircle(sketch, "E609.cCircle", {"center": v(136.3, 346.58) * mm, "radius": 5.72 * mm, "construction": true});
            skLineSegment(sketch, "E609.0", {"start": v(138.04, 340.2) * mm, "end": v(131.65, 341.9) * mm});
            skLineSegment(sketch, "E609.1", {"start": v(131.65, 341.9) * mm, "end": v(129.92, 348.26) * mm});
            skLineSegment(sketch, "E609.2", {"start": v(129.92, 348.26) * mm, "end": v(134.57, 352.95) * mm});
            skLineSegment(sketch, "E609.3", {"start": v(134.57, 352.95) * mm, "end": v(140.95, 351.26) * mm});
            skLineSegment(sketch, "E609.4", {"start": v(140.95, 351.26) * mm, "end": v(142.69, 344.9) * mm});
            skLineSegment(sketch, "E609.5", {"start": v(142.69, 344.9) * mm, "end": v(138.04, 340.2) * mm});
            skPoint(sketch, "E609.0.midPoint", {"position": v(134.84, 341.05) * mm});
            skCircle(sketch, "E610.cCircle", {"center": v(213.2, 331.04) * mm, "radius": 5.03 * mm, "construction": true});
            skLineSegment(sketch, "E610.0", {"start": v(214.33, 325.34) * mm, "end": v(208.83, 327.22) * mm});
            skLineSegment(sketch, "E610.1", {"start": v(208.83, 327.22) * mm, "end": v(207.7, 332.91) * mm});
            skLineSegment(sketch, "E610.2", {"start": v(207.7, 332.91) * mm, "end": v(212.07, 336.74) * mm});
            skLineSegment(sketch, "E610.3", {"start": v(212.07, 336.74) * mm, "end": v(217.57, 334.86) * mm});
            skLineSegment(sketch, "E610.4", {"start": v(217.57, 334.86) * mm, "end": v(218.7, 329.17) * mm});
            skLineSegment(sketch, "E610.5", {"start": v(218.7, 329.17) * mm, "end": v(214.33, 325.34) * mm});
            skPoint(sketch, "E610.0.midPoint", {"position": v(211.58, 326.28) * mm});
            skPoint(sketch, "E611.0.midPoint", {"position": v(179.5, 37.82) * mm});
            skCircle(sketch, "E612.cCircle", {"center": v(206.46, 21.55) * mm, "radius": 8.87 * mm, "construction": true});
            skLineSegment(sketch, "E612.0", {"start": v(215.23, 16.26) * mm, "end": v(206.27, 11.3) * mm});
            skLineSegment(sketch, "E612.1", {"start": v(206.27, 11.3) * mm, "end": v(197.5, 16.59) * mm});
            skLineSegment(sketch, "E612.2", {"start": v(197.5, 16.59) * mm, "end": v(197.68, 26.83) * mm});
            skLineSegment(sketch, "E612.3", {"start": v(197.68, 26.83) * mm, "end": v(206.65, 31.79) * mm});
            skLineSegment(sketch, "E612.4", {"start": v(206.65, 31.79) * mm, "end": v(215.42, 26.5) * mm});
            skLineSegment(sketch, "E612.5", {"start": v(215.42, 26.5) * mm, "end": v(215.23, 16.26) * mm});
            skPoint(sketch, "E612.0.midPoint", {"position": v(210.75, 13.78) * mm});
            skCircle(sketch, "E613.cCircle", {"center": v(241.07, 17.55) * mm, "radius": 10.54 * mm, "construction": true});
            skLineSegment(sketch, "E613.0", {"start": v(250.47, 9.8) * mm, "end": v(239.06, 5.54) * mm});
            skLineSegment(sketch, "E613.1", {"start": v(239.06, 5.54) * mm, "end": v(229.67, 13.28) * mm});
            skLineSegment(sketch, "E613.2", {"start": v(229.67, 13.28) * mm, "end": v(231.68, 25.29) * mm});
            skLineSegment(sketch, "E613.3", {"start": v(231.68, 25.29) * mm, "end": v(243.08, 29.55) * mm});
            skLineSegment(sketch, "E613.4", {"start": v(243.08, 29.55) * mm, "end": v(252.47, 21.8) * mm});
            skLineSegment(sketch, "E613.5", {"start": v(252.47, 21.8) * mm, "end": v(250.47, 9.8) * mm});
            skPoint(sketch, "E613.0.midPoint", {"position": v(244.76, 7.67) * mm});
            skPoint(sketch, "E614.0.midPoint", {"position": v(280.83, 7.33) * mm});
            skPoint(sketch, "E615.0.midPoint", {"position": v(316.97, 6.04) * mm});
            skCircle(sketch, "E616.cCircle", {"center": v(356.21, 17.03) * mm, "radius": 11.6 * mm, "construction": true});
            skLineSegment(sketch, "E616.0", {"start": v(360.26, 4.26) * mm, "end": v(347.18, 7.13) * mm});
            skLineSegment(sketch, "E616.1", {"start": v(347.18, 7.13) * mm, "end": v(343.12, 19.9) * mm});
            skLineSegment(sketch, "E616.2", {"start": v(343.12, 19.9) * mm, "end": v(352.16, 29.8) * mm});
            skLineSegment(sketch, "E616.3", {"start": v(352.16, 29.8) * mm, "end": v(365.24, 26.93) * mm});
            skLineSegment(sketch, "E616.4", {"start": v(365.24, 26.93) * mm, "end": v(369.3, 14.16) * mm});
            skLineSegment(sketch, "E616.5", {"start": v(369.3, 14.16) * mm, "end": v(360.26, 4.26) * mm});
            skPoint(sketch, "E616.0.midPoint", {"position": v(353.72, 5.7) * mm});
            skCircle(sketch, "E617.cCircle", {"center": v(391.67, 22.01) * mm, "radius": 10.43 * mm, "construction": true});
            skLineSegment(sketch, "E617.0", {"start": v(393.72, 10.14) * mm, "end": v(382.41, 14.3) * mm});
            skLineSegment(sketch, "E617.1", {"start": v(382.41, 14.3) * mm, "end": v(380.37, 26.17) * mm});
            skLineSegment(sketch, "E617.2", {"start": v(380.37, 26.17) * mm, "end": v(389.63, 33.88) * mm});
            skLineSegment(sketch, "E617.3", {"start": v(389.63, 33.88) * mm, "end": v(400.93, 29.72) * mm});
            skLineSegment(sketch, "E617.4", {"start": v(400.93, 29.72) * mm, "end": v(402.97, 17.85) * mm});
            skLineSegment(sketch, "E617.5", {"start": v(402.97, 17.85) * mm, "end": v(393.72, 10.14) * mm});
            skPoint(sketch, "E617.0.midPoint", {"position": v(388.06, 12.22) * mm});
            skCircle(sketch, "E618.cCircle", {"center": v(426.79, 20.04) * mm, "radius": 8.8 * mm, "construction": true});
            skLineSegment(sketch, "E618.0", {"start": v(427.48, 9.9) * mm, "end": v(418.36, 14.37) * mm});
            skLineSegment(sketch, "E618.1", {"start": v(418.36, 14.37) * mm, "end": v(417.67, 24.5) * mm});
            skLineSegment(sketch, "E618.2", {"start": v(417.67, 24.5) * mm, "end": v(426.1, 30.17) * mm});
            skLineSegment(sketch, "E618.3", {"start": v(426.1, 30.17) * mm, "end": v(435.21, 25.7) * mm});
            skLineSegment(sketch, "E618.4", {"start": v(435.21, 25.7) * mm, "end": v(435.9, 15.57) * mm});
            skLineSegment(sketch, "E618.5", {"start": v(435.9, 15.57) * mm, "end": v(427.48, 9.9) * mm});
            skPoint(sketch, "E618.0.midPoint", {"position": v(422.92, 12.14) * mm});
            skCircle(sketch, "E619.cCircle", {"center": v(458.38, 40.56) * mm, "radius": 6.97 * mm, "construction": true});
            skLineSegment(sketch, "E619.0", {"start": v(458.33, 32.51) * mm, "end": v(451.4, 36.58) * mm});
            skLineSegment(sketch, "E619.1", {"start": v(451.4, 36.58) * mm, "end": v(451.44, 44.62) * mm});
            skLineSegment(sketch, "E619.2", {"start": v(451.44, 44.62) * mm, "end": v(458.43, 48.6) * mm});
            skLineSegment(sketch, "E619.3", {"start": v(458.43, 48.6) * mm, "end": v(465.37, 44.53) * mm});
            skLineSegment(sketch, "E619.4", {"start": v(465.37, 44.53) * mm, "end": v(465.32, 36.5) * mm});
            skLineSegment(sketch, "E619.5", {"start": v(465.32, 36.5) * mm, "end": v(458.33, 32.51) * mm});
            skPoint(sketch, "E619.0.midPoint", {"position": v(454.86, 34.55) * mm});
            skCircle(sketch, "E620.cCircle", {"center": v(336.08, 99.6) * mm, "radius": 3.93 * mm, "construction": true});
            skLineSegment(sketch, "E620.0", {"start": v(336.25, 95.05) * mm, "end": v(332.24, 97.18) * mm});
            skLineSegment(sketch, "E620.1", {"start": v(332.24, 97.18) * mm, "end": v(332.07, 101.72) * mm});
            skLineSegment(sketch, "E620.2", {"start": v(332.07, 101.72) * mm, "end": v(335.92, 104.13) * mm});
            skLineSegment(sketch, "E620.3", {"start": v(335.92, 104.13) * mm, "end": v(339.93, 102) * mm});
            skLineSegment(sketch, "E620.4", {"start": v(339.93, 102) * mm, "end": v(340.1, 97.47) * mm});
            skLineSegment(sketch, "E620.5", {"start": v(340.1, 97.47) * mm, "end": v(336.25, 95.05) * mm});
            skPoint(sketch, "E620.0.midPoint", {"position": v(334.24, 96.12) * mm});
            skCircle(sketch, "E621.cCircle", {"center": v(299.4, 89.36) * mm, "radius": 4.18 * mm, "construction": true});
            skLineSegment(sketch, "E621.0", {"start": v(303.42, 86.7) * mm, "end": v(299.1, 84.55) * mm});
            skLineSegment(sketch, "E621.1", {"start": v(299.1, 84.55) * mm, "end": v(295.08, 87.22) * mm});
            skLineSegment(sketch, "E621.2", {"start": v(295.08, 87.22) * mm, "end": v(295.4, 92.04) * mm});
            skLineSegment(sketch, "E621.3", {"start": v(295.4, 92.04) * mm, "end": v(299.71, 94.18) * mm});
            skLineSegment(sketch, "E621.4", {"start": v(299.71, 94.18) * mm, "end": v(303.73, 91.5) * mm});
            skLineSegment(sketch, "E621.5", {"start": v(303.73, 91.5) * mm, "end": v(303.42, 86.7) * mm});
            skPoint(sketch, "E621.0.midPoint", {"position": v(301.26, 85.62) * mm});
            skCircle(sketch, "E622.cCircle", {"center": v(525.06, 269.24) * mm, "radius": 8.31 * mm, "construction": true});
            skLineSegment(sketch, "E622.0", {"start": v(529.86, 260.93) * mm, "end": v(520.26, 260.93) * mm});
            skLineSegment(sketch, "E622.1", {"start": v(520.26, 260.93) * mm, "end": v(515.46, 269.24) * mm});
            skLineSegment(sketch, "E622.2", {"start": v(515.46, 269.24) * mm, "end": v(520.26, 277.55) * mm});
            skLineSegment(sketch, "E622.3", {"start": v(520.26, 277.55) * mm, "end": v(529.86, 277.55) * mm});
            skLineSegment(sketch, "E622.4", {"start": v(529.86, 277.55) * mm, "end": v(534.66, 269.24) * mm});
            skLineSegment(sketch, "E622.5", {"start": v(534.66, 269.24) * mm, "end": v(529.86, 260.93) * mm});
            skPoint(sketch, "E622.0.midPoint", {"position": v(525.06, 260.93) * mm});
            skCircle(sketch, "E623.cCircle", {"center": v(549.18, 283.96) * mm, "radius": 6.81 * mm, "construction": true});
            skLineSegment(sketch, "E623.0", {"start": v(553.12, 277.15) * mm, "end": v(545.25, 277.15) * mm});
            skLineSegment(sketch, "E623.1", {"start": v(545.25, 277.15) * mm, "end": v(541.31, 283.96) * mm});
            skLineSegment(sketch, "E623.2", {"start": v(541.31, 283.96) * mm, "end": v(545.25, 290.77) * mm});
            skLineSegment(sketch, "E623.3", {"start": v(545.25, 290.77) * mm, "end": v(553.12, 290.77) * mm});
            skLineSegment(sketch, "E623.4", {"start": v(553.12, 290.77) * mm, "end": v(557.05, 283.96) * mm});
            skLineSegment(sketch, "E623.5", {"start": v(557.05, 283.96) * mm, "end": v(553.12, 277.15) * mm});
            skPoint(sketch, "E623.0.midPoint", {"position": v(549.18, 277.15) * mm});
            skCircle(sketch, "E624.cCircle", {"center": v(498.75, 296.77) * mm, "radius": 5.86 * mm, "construction": true});
            skLineSegment(sketch, "E624.0", {"start": v(502.14, 290.91) * mm, "end": v(495.37, 290.91) * mm});
            skLineSegment(sketch, "E624.1", {"start": v(495.37, 290.91) * mm, "end": v(491.98, 296.77) * mm});
            skLineSegment(sketch, "E624.2", {"start": v(491.98, 296.77) * mm, "end": v(495.37, 302.63) * mm});
            skLineSegment(sketch, "E624.3", {"start": v(495.37, 302.63) * mm, "end": v(502.14, 302.63) * mm});
            skLineSegment(sketch, "E624.4", {"start": v(502.14, 302.63) * mm, "end": v(505.52, 296.77) * mm});
            skLineSegment(sketch, "E624.5", {"start": v(505.52, 296.77) * mm, "end": v(502.14, 290.91) * mm});
            skPoint(sketch, "E624.0.midPoint", {"position": v(498.75, 290.91) * mm});
            skCircle(sketch, "E625.cCircle", {"center": v(417.37, 320.96) * mm, "radius": 6.37 * mm, "construction": true});
            skLineSegment(sketch, "E625.0", {"start": v(421.05, 314.6) * mm, "end": v(413.7, 314.6) * mm});
            skLineSegment(sketch, "E625.1", {"start": v(413.7, 314.6) * mm, "end": v(410.02, 320.96) * mm});
            skLineSegment(sketch, "E625.2", {"start": v(410.02, 320.96) * mm, "end": v(413.7, 327.33) * mm});
            skLineSegment(sketch, "E625.3", {"start": v(413.7, 327.33) * mm, "end": v(421.05, 327.33) * mm});
            skLineSegment(sketch, "E625.4", {"start": v(421.05, 327.33) * mm, "end": v(424.72, 320.96) * mm});
            skLineSegment(sketch, "E625.5", {"start": v(424.72, 320.96) * mm, "end": v(421.05, 314.6) * mm});
            skPoint(sketch, "E625.0.midPoint", {"position": v(417.37, 314.6) * mm});
            skCircle(sketch, "E626.cCircle", {"center": v(346.25, 347.9) * mm, "radius": 5.32 * mm, "construction": true});
            skLineSegment(sketch, "E626.0", {"start": v(349.32, 342.58) * mm, "end": v(343.18, 342.58) * mm});
            skLineSegment(sketch, "E626.1", {"start": v(343.18, 342.58) * mm, "end": v(340.11, 347.9) * mm});
            skLineSegment(sketch, "E626.2", {"start": v(340.11, 347.9) * mm, "end": v(343.18, 353.22) * mm});
            skLineSegment(sketch, "E626.3", {"start": v(343.18, 353.22) * mm, "end": v(349.32, 353.22) * mm});
            skLineSegment(sketch, "E626.4", {"start": v(349.32, 353.22) * mm, "end": v(352.39, 347.9) * mm});
            skLineSegment(sketch, "E626.5", {"start": v(352.39, 347.9) * mm, "end": v(349.32, 342.58) * mm});
            skPoint(sketch, "E626.0.midPoint", {"position": v(346.25, 342.58) * mm});
            skCircle(sketch, "E627.cCircle", {"center": v(320.91, 322.09) * mm, "radius": 5.1 * mm, "construction": true});
            skLineSegment(sketch, "E627.0", {"start": v(323.86, 316.98) * mm, "end": v(317.96, 316.98) * mm});
            skLineSegment(sketch, "E627.1", {"start": v(317.96, 316.98) * mm, "end": v(315.01, 322.09) * mm});
            skLineSegment(sketch, "E627.2", {"start": v(315.01, 322.09) * mm, "end": v(317.96, 327.2) * mm});
            skLineSegment(sketch, "E627.3", {"start": v(317.96, 327.2) * mm, "end": v(323.86, 327.2) * mm});
            skLineSegment(sketch, "E627.4", {"start": v(323.86, 327.2) * mm, "end": v(326.81, 322.09) * mm});
            skLineSegment(sketch, "E627.5", {"start": v(326.81, 322.09) * mm, "end": v(323.86, 316.98) * mm});
            skPoint(sketch, "E627.0.midPoint", {"position": v(320.91, 316.98) * mm});
            skCircle(sketch, "E628.cCircle", {"center": v(308.19, 347.08) * mm, "radius": 5.7 * mm, "construction": true});
            skLineSegment(sketch, "E628.0", {"start": v(312, 341.71) * mm, "end": v(305.45, 341.09) * mm});
            skLineSegment(sketch, "E628.1", {"start": v(305.45, 341.09) * mm, "end": v(301.63, 346.45) * mm});
            skLineSegment(sketch, "E628.2", {"start": v(301.63, 346.45) * mm, "end": v(304.37, 352.44) * mm});
            skLineSegment(sketch, "E628.3", {"start": v(304.37, 352.44) * mm, "end": v(310.93, 353.07) * mm});
            skLineSegment(sketch, "E628.4", {"start": v(310.93, 353.07) * mm, "end": v(314.75, 347.7) * mm});
            skLineSegment(sketch, "E628.5", {"start": v(314.75, 347.7) * mm, "end": v(312, 341.71) * mm});
            skPoint(sketch, "E628.0.midPoint", {"position": v(308.73, 341.4) * mm});
            skCircle(sketch, "E629.cCircle", {"center": v(346.25, 275.8) * mm, "radius": 6.99 * mm, "construction": true});
            skLineSegment(sketch, "E629.0", {"start": v(348.64, 268.1) * mm, "end": v(340.77, 269.88) * mm});
            skLineSegment(sketch, "E629.1", {"start": v(340.77, 269.88) * mm, "end": v(338.38, 277.59) * mm});
            skLineSegment(sketch, "E629.2", {"start": v(338.38, 277.59) * mm, "end": v(343.86, 283.5) * mm});
            skLineSegment(sketch, "E629.3", {"start": v(343.86, 283.5) * mm, "end": v(351.73, 281.72) * mm});
            skLineSegment(sketch, "E629.4", {"start": v(351.73, 281.72) * mm, "end": v(354.12, 274.01) * mm});
            skLineSegment(sketch, "E629.5", {"start": v(354.12, 274.01) * mm, "end": v(348.64, 268.1) * mm});
            skPoint(sketch, "E629.0.midPoint", {"position": v(344.7, 268.98) * mm});
            skCircle(sketch, "E630.cCircle", {"center": v(289.78, 274.1) * mm, "radius": 7.75 * mm, "construction": true});
            skLineSegment(sketch, "E630.0", {"start": v(295.1, 266.9) * mm, "end": v(286.22, 265.88) * mm});
            skLineSegment(sketch, "E630.1", {"start": v(286.22, 265.88) * mm, "end": v(280.88, 273.07) * mm});
            skLineSegment(sketch, "E630.2", {"start": v(280.88, 273.07) * mm, "end": v(284.44, 281.28) * mm});
            skLineSegment(sketch, "E630.3", {"start": v(284.44, 281.28) * mm, "end": v(293.34, 282.3) * mm});
            skLineSegment(sketch, "E630.4", {"start": v(293.34, 282.3) * mm, "end": v(298.67, 275.12) * mm});
            skLineSegment(sketch, "E630.5", {"start": v(298.67, 275.12) * mm, "end": v(295.1, 266.9) * mm});
            skPoint(sketch, "E630.0.midPoint", {"position": v(290.66, 266.4) * mm});
            skCircle(sketch, "E631.cCircle", {"center": v(448.15, 482.94) * mm, "radius": 8.9 * mm, "construction": true});
            skLineSegment(sketch, "E631.0", {"start": v(454.73, 475.05) * mm, "end": v(444.6, 473.3) * mm});
            skLineSegment(sketch, "E631.1", {"start": v(444.6, 473.3) * mm, "end": v(438.03, 481.18) * mm});
            skLineSegment(sketch, "E631.2", {"start": v(438.03, 481.18) * mm, "end": v(441.57, 490.82) * mm});
            skLineSegment(sketch, "E631.3", {"start": v(441.57, 490.82) * mm, "end": v(451.68, 492.58) * mm});
            skLineSegment(sketch, "E631.4", {"start": v(451.68, 492.58) * mm, "end": v(458.26, 484.7) * mm});
            skLineSegment(sketch, "E631.5", {"start": v(458.26, 484.7) * mm, "end": v(454.73, 475.05) * mm});
            skPoint(sketch, "E631.0.midPoint", {"position": v(449.67, 474.18) * mm});
            skCircle(sketch, "E632.cCircle", {"center": v(316.37, 17.46) * mm, "radius": 14.21 * mm, "construction": true});
            skLineSegment(sketch, "E632.0", {"start": v(324.84, 3.4) * mm, "end": v(308.43, 3.1) * mm});
            skLineSegment(sketch, "E632.1", {"start": v(308.43, 3.1) * mm, "end": v(299.97, 17.15) * mm});
            skLineSegment(sketch, "E632.2", {"start": v(299.97, 17.15) * mm, "end": v(307.9, 31.51) * mm});
            skLineSegment(sketch, "E632.3", {"start": v(307.9, 31.51) * mm, "end": v(324.3, 31.82) * mm});
            skLineSegment(sketch, "E632.4", {"start": v(324.3, 31.82) * mm, "end": v(332.78, 17.77) * mm});
            skLineSegment(sketch, "E632.5", {"start": v(332.78, 17.77) * mm, "end": v(324.84, 3.4) * mm});
            skPoint(sketch, "E632.0.midPoint", {"position": v(316.64, 3.25) * mm});
            skCircle(sketch, "E633.cCircle", {"center": v(277.73, 18.15) * mm, "radius": 12.36 * mm, "construction": true});
            skLineSegment(sketch, "E633.0", {"start": v(287.74, 7.96) * mm, "end": v(273.92, 4.4) * mm});
            skLineSegment(sketch, "E633.1", {"start": v(273.92, 4.4) * mm, "end": v(263.91, 14.58) * mm});
            skLineSegment(sketch, "E633.2", {"start": v(263.91, 14.58) * mm, "end": v(267.73, 28.33) * mm});
            skLineSegment(sketch, "E633.3", {"start": v(267.73, 28.33) * mm, "end": v(281.55, 31.9) * mm});
            skLineSegment(sketch, "E633.4", {"start": v(281.55, 31.9) * mm, "end": v(291.55, 21.72) * mm});
            skLineSegment(sketch, "E633.5", {"start": v(291.55, 21.72) * mm, "end": v(287.74, 7.96) * mm});
            skPoint(sketch, "E633.0.midPoint", {"position": v(280.83, 6.18) * mm});
            skCircle(sketch, "E634.cCircle", {"center": v(176.48, 43) * mm, "radius": 7.16 * mm, "construction": true});
            skLineSegment(sketch, "E634.0", {"start": v(183.66, 38.9) * mm, "end": v(176.5, 34.74) * mm});
            skLineSegment(sketch, "E634.1", {"start": v(176.5, 34.74) * mm, "end": v(169.33, 38.85) * mm});
            skLineSegment(sketch, "E634.2", {"start": v(169.33, 38.85) * mm, "end": v(169.3, 47.12) * mm});
            skLineSegment(sketch, "E634.3", {"start": v(169.3, 47.12) * mm, "end": v(176.45, 51.28) * mm});
            skLineSegment(sketch, "E634.4", {"start": v(176.45, 51.28) * mm, "end": v(183.63, 47.17) * mm});
            skLineSegment(sketch, "E634.5", {"start": v(183.63, 47.17) * mm, "end": v(183.66, 38.9) * mm});
            skPoint(sketch, "E634.0.midPoint", {"position": v(180.08, 36.82) * mm});
            skLineSegment(sketch, "E635", {"start": v(348.41, 319.52) * mm, "end": v(353.1, 340.13) * mm});
            skLineSegment(sketch, "E636", {"start": v(340.94, 338.35) * mm, "end": v(339.54, 336.96) * mm});
            skLineSegment(sketch, "E637", {"start": v(337.47, 342.35) * mm, "end": v(335.49, 340.82) * mm});
            skArc(sketch, "E638.trimOffspring", {"start": v(335.49, 340.82) * mm, "mid": v(332.63, 342.94) * mm, "end": v(329.58, 344.79) * mm});
            skLineSegment(sketch, "E639", {"start": v(411.98, 424.25) * mm, "end": v(412.29, 424.61) * mm});
            skLineSegment(sketch, "E640", {"start": v(411.98, 416.8) * mm, "end": v(410.85, 417.67) * mm});
            skLineSegment(sketch, "E641", {"start": v(537.22, 179.3) * mm, "end": v(537.33, 179.5) * mm});
            skSolve(sketch);
        }
        {
            var Q0;
            Q0=makeQuery(id+"F0.imprint","IMPRINT",FACE,{"disambiguationData":[TD([[makeQuery(id+"F0.imprint","IMPRINT",EDGE,{"derivedFrom":sQuery(id+"F0.wireOp",EDGE,"E0")}),1.0]])]});
            extrude(context, id + "F1", {"entities" : qUnion([Q0]), "depth" : 6.35 * mm, "offsetDistance" : 25.4 * mm});
        }
    });
